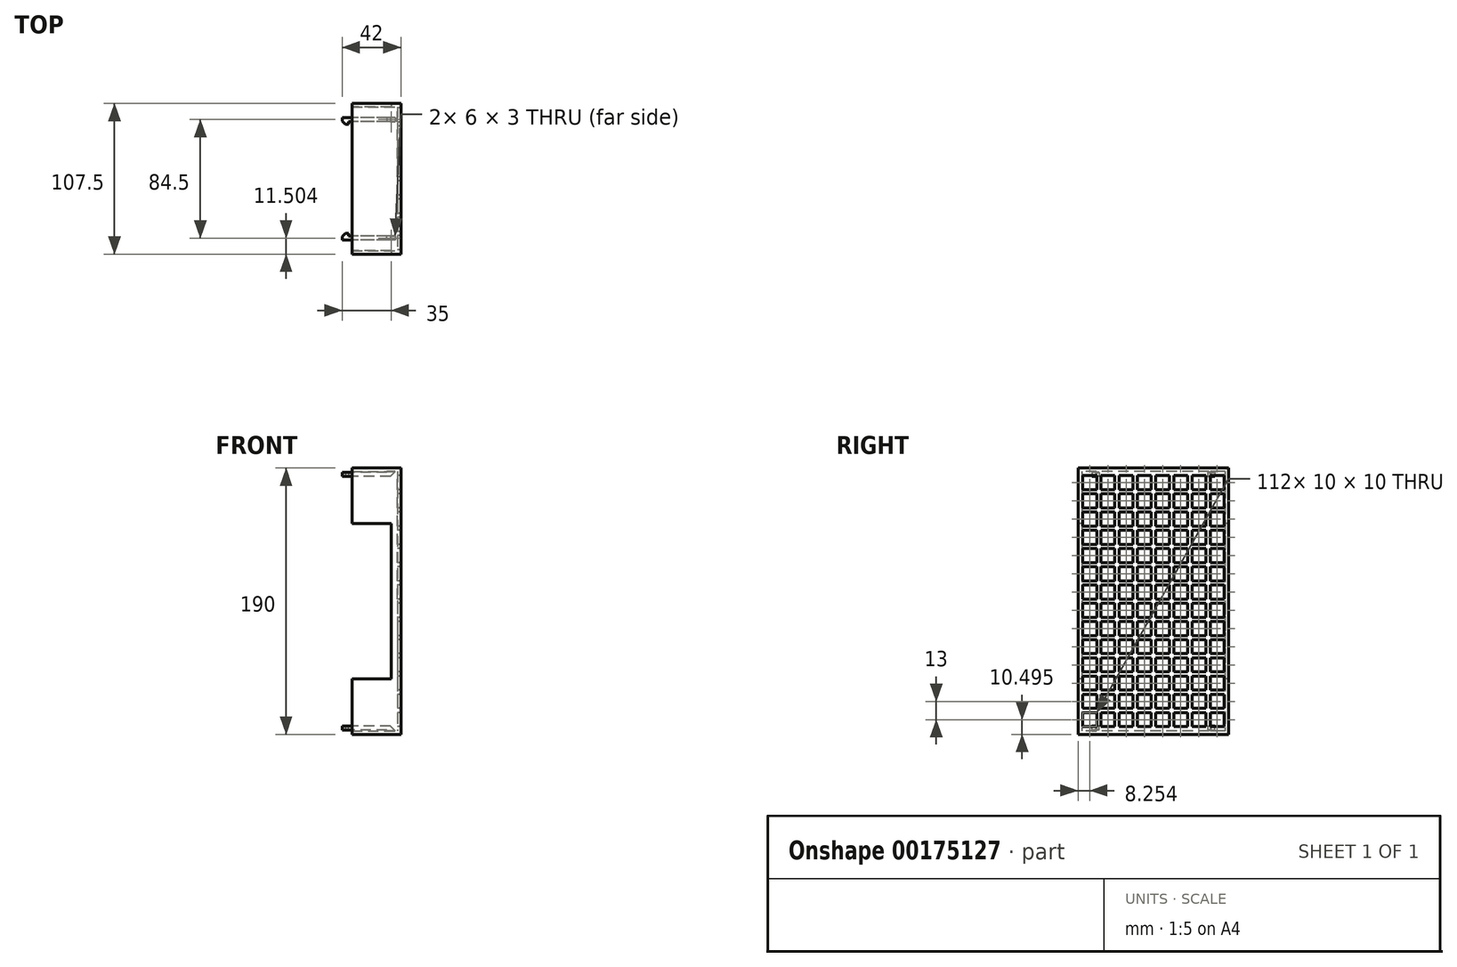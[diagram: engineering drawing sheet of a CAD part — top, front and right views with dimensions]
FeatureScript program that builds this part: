
annotation { "Feature Type Name" : "Feature", "Feature Type Description" : "" }
export const myFeature = defineFeature(function(context is Context, id is Id, definition is map)
    precondition{}
    {
        {
            var Q0;
            Q0=qCreatedBy(makeId("Right.planeOp"),FACE);
            var sketch = newSketch(context, id + "F0", { "sketchPlane" : qUnion([Q0])});
            skLineSegment(sketch, "E0.bottom", {"start": v(-54.49, 123.63) * mm, "end": v(53.01, 123.63) * mm});
            skLineSegment(sketch, "E0.top", {"start": v(-54.49, -66.37) * mm, "end": v(53.01, -66.37) * mm});
            skLineSegment(sketch, "E0.left", {"start": v(-54.49, 123.63) * mm, "end": v(-54.49, -66.37) * mm});
            skLineSegment(sketch, "E0.right", {"start": v(53.01, 123.63) * mm, "end": v(53.01, -66.37) * mm});
            skLineSegment(sketch, "E1.bottom", {"start": v(-2.24, 30.13) * mm, "end": v(-12.24, 30.13) * mm});
            skLineSegment(sketch, "E1.top", {"start": v(-2.24, 40.13) * mm, "end": v(-12.24, 40.13) * mm});
            skLineSegment(sketch, "E1.left", {"start": v(-2.24, 30.13) * mm, "end": v(-2.24, 40.13) * mm});
            skLineSegment(sketch, "E1.right", {"start": v(-12.24, 30.13) * mm, "end": v(-12.24, 40.13) * mm});
            skLineSegment(sketch, "E2.0.1.0", {"start": v(-2.24, 43.13) * mm, "end": v(-2.24, 53.13) * mm});
            skLineSegment(sketch, "E2.0.1.1", {"start": v(-12.24, 43.13) * mm, "end": v(-12.24, 53.13) * mm});
            skLineSegment(sketch, "E2.0.1.2", {"start": v(-2.24, 43.13) * mm, "end": v(-12.24, 43.13) * mm});
            skLineSegment(sketch, "E2.0.1.3", {"start": v(-2.24, 53.13) * mm, "end": v(-12.24, 53.13) * mm});
            skLineSegment(sketch, "E2.0.2.0", {"start": v(-2.24, 56.13) * mm, "end": v(-2.24, 66.13) * mm});
            skLineSegment(sketch, "E2.0.2.1", {"start": v(-12.24, 56.13) * mm, "end": v(-12.24, 66.13) * mm});
            skLineSegment(sketch, "E2.0.2.2", {"start": v(-2.24, 56.13) * mm, "end": v(-12.24, 56.13) * mm});
            skLineSegment(sketch, "E2.0.2.3", {"start": v(-2.24, 66.13) * mm, "end": v(-12.24, 66.13) * mm});
            skLineSegment(sketch, "E2.0.3.0", {"start": v(-2.24, 69.13) * mm, "end": v(-2.24, 79.13) * mm});
            skLineSegment(sketch, "E2.0.3.1", {"start": v(-12.24, 69.13) * mm, "end": v(-12.24, 79.13) * mm});
            skLineSegment(sketch, "E2.0.3.2", {"start": v(-2.24, 69.13) * mm, "end": v(-12.24, 69.13) * mm});
            skLineSegment(sketch, "E2.0.3.3", {"start": v(-2.24, 79.13) * mm, "end": v(-12.24, 79.13) * mm});
            skLineSegment(sketch, "E2.0.4.0", {"start": v(-2.24, 82.13) * mm, "end": v(-2.24, 92.13) * mm});
            skLineSegment(sketch, "E2.0.4.1", {"start": v(-12.24, 82.13) * mm, "end": v(-12.24, 92.13) * mm});
            skLineSegment(sketch, "E2.0.4.2", {"start": v(-2.24, 82.13) * mm, "end": v(-12.24, 82.13) * mm});
            skLineSegment(sketch, "E2.0.4.3", {"start": v(-2.24, 92.13) * mm, "end": v(-12.24, 92.13) * mm});
            skLineSegment(sketch, "E2.0.5.0", {"start": v(-2.24, 95.13) * mm, "end": v(-2.24, 105.13) * mm});
            skLineSegment(sketch, "E2.0.5.1", {"start": v(-12.24, 95.13) * mm, "end": v(-12.24, 105.13) * mm});
            skLineSegment(sketch, "E2.0.5.2", {"start": v(-2.24, 95.13) * mm, "end": v(-12.24, 95.13) * mm});
            skLineSegment(sketch, "E2.0.5.3", {"start": v(-2.24, 105.13) * mm, "end": v(-12.24, 105.13) * mm});
            skLineSegment(sketch, "E2.0.6.0", {"start": v(-2.24, 108.13) * mm, "end": v(-2.24, 118.13) * mm});
            skLineSegment(sketch, "E2.0.6.1", {"start": v(-12.24, 108.13) * mm, "end": v(-12.24, 118.13) * mm});
            skLineSegment(sketch, "E2.0.6.2", {"start": v(-2.24, 108.13) * mm, "end": v(-12.24, 108.13) * mm});
            skLineSegment(sketch, "E2.0.6.3", {"start": v(-2.24, 118.13) * mm, "end": v(-12.24, 118.13) * mm});
            skLineSegment(sketch, "E2.1.0.0", {"start": v(-15.24, 30.13) * mm, "end": v(-15.24, 40.13) * mm});
            skLineSegment(sketch, "E2.1.0.1", {"start": v(-25.24, 30.13) * mm, "end": v(-25.24, 40.13) * mm});
            skLineSegment(sketch, "E2.1.0.2", {"start": v(-15.24, 30.13) * mm, "end": v(-25.24, 30.13) * mm});
            skLineSegment(sketch, "E2.1.0.3", {"start": v(-15.24, 40.13) * mm, "end": v(-25.24, 40.13) * mm});
            skLineSegment(sketch, "E2.1.1.0", {"start": v(-15.24, 43.13) * mm, "end": v(-15.24, 53.13) * mm});
            skLineSegment(sketch, "E2.1.1.1", {"start": v(-25.24, 43.13) * mm, "end": v(-25.24, 53.13) * mm});
            skLineSegment(sketch, "E2.1.1.2", {"start": v(-15.24, 43.13) * mm, "end": v(-25.24, 43.13) * mm});
            skLineSegment(sketch, "E2.1.1.3", {"start": v(-15.24, 53.13) * mm, "end": v(-25.24, 53.13) * mm});
            skLineSegment(sketch, "E2.1.2.0", {"start": v(-15.24, 56.13) * mm, "end": v(-15.24, 66.13) * mm});
            skLineSegment(sketch, "E2.1.2.1", {"start": v(-25.24, 56.13) * mm, "end": v(-25.24, 66.13) * mm});
            skLineSegment(sketch, "E2.1.2.2", {"start": v(-15.24, 56.13) * mm, "end": v(-25.24, 56.13) * mm});
            skLineSegment(sketch, "E2.1.2.3", {"start": v(-15.24, 66.13) * mm, "end": v(-25.24, 66.13) * mm});
            skLineSegment(sketch, "E2.1.3.0", {"start": v(-15.24, 69.13) * mm, "end": v(-15.24, 79.13) * mm});
            skLineSegment(sketch, "E2.1.3.1", {"start": v(-25.24, 69.13) * mm, "end": v(-25.24, 79.13) * mm});
            skLineSegment(sketch, "E2.1.3.2", {"start": v(-15.24, 69.13) * mm, "end": v(-25.24, 69.13) * mm});
            skLineSegment(sketch, "E2.1.3.3", {"start": v(-15.24, 79.13) * mm, "end": v(-25.24, 79.13) * mm});
            skLineSegment(sketch, "E2.1.4.0", {"start": v(-15.24, 82.13) * mm, "end": v(-15.24, 92.13) * mm});
            skLineSegment(sketch, "E2.1.4.1", {"start": v(-25.24, 82.13) * mm, "end": v(-25.24, 92.13) * mm});
            skLineSegment(sketch, "E2.1.4.2", {"start": v(-15.24, 82.13) * mm, "end": v(-25.24, 82.13) * mm});
            skLineSegment(sketch, "E2.1.4.3", {"start": v(-15.24, 92.13) * mm, "end": v(-25.24, 92.13) * mm});
            skLineSegment(sketch, "E2.1.5.0", {"start": v(-15.24, 95.13) * mm, "end": v(-15.24, 105.13) * mm});
            skLineSegment(sketch, "E2.1.5.1", {"start": v(-25.24, 95.13) * mm, "end": v(-25.24, 105.13) * mm});
            skLineSegment(sketch, "E2.1.5.2", {"start": v(-15.24, 95.13) * mm, "end": v(-25.24, 95.13) * mm});
            skLineSegment(sketch, "E2.1.5.3", {"start": v(-15.24, 105.13) * mm, "end": v(-25.24, 105.13) * mm});
            skLineSegment(sketch, "E2.1.6.0", {"start": v(-15.24, 108.13) * mm, "end": v(-15.24, 118.13) * mm});
            skLineSegment(sketch, "E2.1.6.1", {"start": v(-25.24, 108.13) * mm, "end": v(-25.24, 118.13) * mm});
            skLineSegment(sketch, "E2.1.6.2", {"start": v(-15.24, 108.13) * mm, "end": v(-25.24, 108.13) * mm});
            skLineSegment(sketch, "E2.1.6.3", {"start": v(-15.24, 118.13) * mm, "end": v(-25.24, 118.13) * mm});
            skLineSegment(sketch, "E2.2.0.0", {"start": v(-28.24, 30.13) * mm, "end": v(-28.24, 40.13) * mm});
            skLineSegment(sketch, "E2.2.0.1", {"start": v(-38.24, 30.13) * mm, "end": v(-38.24, 40.13) * mm});
            skLineSegment(sketch, "E2.2.0.2", {"start": v(-28.24, 30.13) * mm, "end": v(-38.24, 30.13) * mm});
            skLineSegment(sketch, "E2.2.0.3", {"start": v(-28.24, 40.13) * mm, "end": v(-38.24, 40.13) * mm});
            skLineSegment(sketch, "E2.2.1.0", {"start": v(-28.24, 43.13) * mm, "end": v(-28.24, 53.13) * mm});
            skLineSegment(sketch, "E2.2.1.1", {"start": v(-38.24, 43.13) * mm, "end": v(-38.24, 53.13) * mm});
            skLineSegment(sketch, "E2.2.1.2", {"start": v(-28.24, 43.13) * mm, "end": v(-38.24, 43.13) * mm});
            skLineSegment(sketch, "E2.2.1.3", {"start": v(-28.24, 53.13) * mm, "end": v(-38.24, 53.13) * mm});
            skLineSegment(sketch, "E2.2.2.0", {"start": v(-28.24, 56.13) * mm, "end": v(-28.24, 66.13) * mm});
            skLineSegment(sketch, "E2.2.2.1", {"start": v(-38.24, 56.13) * mm, "end": v(-38.24, 66.13) * mm});
            skLineSegment(sketch, "E2.2.2.2", {"start": v(-28.24, 56.13) * mm, "end": v(-38.24, 56.13) * mm});
            skLineSegment(sketch, "E2.2.2.3", {"start": v(-28.24, 66.13) * mm, "end": v(-38.24, 66.13) * mm});
            skLineSegment(sketch, "E2.2.3.0", {"start": v(-28.24, 69.13) * mm, "end": v(-28.24, 79.13) * mm});
            skLineSegment(sketch, "E2.2.3.1", {"start": v(-38.24, 69.13) * mm, "end": v(-38.24, 79.13) * mm});
            skLineSegment(sketch, "E2.2.3.2", {"start": v(-28.24, 69.13) * mm, "end": v(-38.24, 69.13) * mm});
            skLineSegment(sketch, "E2.2.3.3", {"start": v(-28.24, 79.13) * mm, "end": v(-38.24, 79.13) * mm});
            skLineSegment(sketch, "E2.2.4.0", {"start": v(-28.24, 82.13) * mm, "end": v(-28.24, 92.13) * mm});
            skLineSegment(sketch, "E2.2.4.1", {"start": v(-38.24, 82.13) * mm, "end": v(-38.24, 92.13) * mm});
            skLineSegment(sketch, "E2.2.4.2", {"start": v(-28.24, 82.13) * mm, "end": v(-38.24, 82.13) * mm});
            skLineSegment(sketch, "E2.2.4.3", {"start": v(-28.24, 92.13) * mm, "end": v(-38.24, 92.13) * mm});
            skLineSegment(sketch, "E2.2.5.0", {"start": v(-28.24, 95.13) * mm, "end": v(-28.24, 105.13) * mm});
            skLineSegment(sketch, "E2.2.5.1", {"start": v(-38.24, 95.13) * mm, "end": v(-38.24, 105.13) * mm});
            skLineSegment(sketch, "E2.2.5.2", {"start": v(-28.24, 95.13) * mm, "end": v(-38.24, 95.13) * mm});
            skLineSegment(sketch, "E2.2.5.3", {"start": v(-28.24, 105.13) * mm, "end": v(-38.24, 105.13) * mm});
            skLineSegment(sketch, "E2.2.6.0", {"start": v(-28.24, 108.13) * mm, "end": v(-28.24, 118.13) * mm});
            skLineSegment(sketch, "E2.2.6.1", {"start": v(-38.24, 108.13) * mm, "end": v(-38.24, 118.13) * mm});
            skLineSegment(sketch, "E2.2.6.2", {"start": v(-28.24, 108.13) * mm, "end": v(-38.24, 108.13) * mm});
            skLineSegment(sketch, "E2.2.6.3", {"start": v(-28.24, 118.13) * mm, "end": v(-38.24, 118.13) * mm});
            skLineSegment(sketch, "E2.3.0.0", {"start": v(-41.24, 30.13) * mm, "end": v(-41.24, 40.13) * mm});
            skLineSegment(sketch, "E2.3.0.1", {"start": v(-51.24, 30.13) * mm, "end": v(-51.24, 40.13) * mm});
            skLineSegment(sketch, "E2.3.0.2", {"start": v(-41.24, 30.13) * mm, "end": v(-51.24, 30.13) * mm});
            skLineSegment(sketch, "E2.3.0.3", {"start": v(-41.24, 40.13) * mm, "end": v(-51.24, 40.13) * mm});
            skLineSegment(sketch, "E2.3.1.0", {"start": v(-41.24, 43.13) * mm, "end": v(-41.24, 53.13) * mm});
            skLineSegment(sketch, "E2.3.1.1", {"start": v(-51.24, 43.13) * mm, "end": v(-51.24, 53.13) * mm});
            skLineSegment(sketch, "E2.3.1.2", {"start": v(-41.24, 43.13) * mm, "end": v(-51.24, 43.13) * mm});
            skLineSegment(sketch, "E2.3.1.3", {"start": v(-41.24, 53.13) * mm, "end": v(-51.24, 53.13) * mm});
            skLineSegment(sketch, "E2.3.2.0", {"start": v(-41.24, 56.13) * mm, "end": v(-41.24, 66.13) * mm});
            skLineSegment(sketch, "E2.3.2.1", {"start": v(-51.24, 56.13) * mm, "end": v(-51.24, 66.13) * mm});
            skLineSegment(sketch, "E2.3.2.2", {"start": v(-41.24, 56.13) * mm, "end": v(-51.24, 56.13) * mm});
            skLineSegment(sketch, "E2.3.2.3", {"start": v(-41.24, 66.13) * mm, "end": v(-51.24, 66.13) * mm});
            skLineSegment(sketch, "E2.3.3.0", {"start": v(-41.24, 69.13) * mm, "end": v(-41.24, 79.13) * mm});
            skLineSegment(sketch, "E2.3.3.1", {"start": v(-51.24, 69.13) * mm, "end": v(-51.24, 79.13) * mm});
            skLineSegment(sketch, "E2.3.3.2", {"start": v(-41.24, 69.13) * mm, "end": v(-51.24, 69.13) * mm});
            skLineSegment(sketch, "E2.3.3.3", {"start": v(-41.24, 79.13) * mm, "end": v(-51.24, 79.13) * mm});
            skLineSegment(sketch, "E2.3.4.0", {"start": v(-41.24, 82.13) * mm, "end": v(-41.24, 92.13) * mm});
            skLineSegment(sketch, "E2.3.4.1", {"start": v(-51.24, 82.13) * mm, "end": v(-51.24, 92.13) * mm});
            skLineSegment(sketch, "E2.3.4.2", {"start": v(-41.24, 82.13) * mm, "end": v(-51.24, 82.13) * mm});
            skLineSegment(sketch, "E2.3.4.3", {"start": v(-41.24, 92.13) * mm, "end": v(-51.24, 92.13) * mm});
            skLineSegment(sketch, "E2.3.5.0", {"start": v(-41.24, 95.13) * mm, "end": v(-41.24, 105.13) * mm});
            skLineSegment(sketch, "E2.3.5.1", {"start": v(-51.24, 95.13) * mm, "end": v(-51.24, 105.13) * mm});
            skLineSegment(sketch, "E2.3.5.2", {"start": v(-41.24, 95.13) * mm, "end": v(-51.24, 95.13) * mm});
            skLineSegment(sketch, "E2.3.5.3", {"start": v(-41.24, 105.13) * mm, "end": v(-51.24, 105.13) * mm});
            skLineSegment(sketch, "E2.3.6.0", {"start": v(-41.24, 108.13) * mm, "end": v(-41.24, 118.13) * mm});
            skLineSegment(sketch, "E2.3.6.1", {"start": v(-51.24, 108.13) * mm, "end": v(-51.24, 118.13) * mm});
            skLineSegment(sketch, "E2.3.6.2", {"start": v(-41.24, 108.13) * mm, "end": v(-51.24, 108.13) * mm});
            skLineSegment(sketch, "E2.3.6.3", {"start": v(-41.24, 118.13) * mm, "end": v(-51.24, 118.13) * mm});
            skLineSegment(sketch, "E2.direction1", {"start": v(-12.24, 30.13) * mm, "end": v(-25.24, 30.13) * mm, "construction": true});
            skLineSegment(sketch, "E2.direction2", {"start": v(-12.24, 30.13) * mm, "end": v(-12.24, 43.13) * mm, "construction": true});
            skLineSegment(sketch, "E3.MirrorCS", {"start": v(10.76, 30.13) * mm, "end": v(10.76, 40.13) * mm});
            skLineSegment(sketch, "E4.MirrorCS", {"start": v(26.76, 30.13) * mm, "end": v(26.76, 40.13) * mm});
            skLineSegment(sketch, "E5.MirrorCS", {"start": v(13.76, 43.13) * mm, "end": v(23.76, 43.13) * mm});
            skLineSegment(sketch, "E6.MirrorCS", {"start": v(13.76, 40.13) * mm, "end": v(23.76, 40.13) * mm});
            skLineSegment(sketch, "E7.MirrorCS", {"start": v(13.76, 30.13) * mm, "end": v(23.76, 30.13) * mm});
            skLineSegment(sketch, "E8.MirrorCS", {"start": v(23.76, 30.13) * mm, "end": v(23.76, 40.13) * mm});
            skLineSegment(sketch, "E9.MirrorCS", {"start": v(26.76, 79.13) * mm, "end": v(36.76, 79.13) * mm});
            skLineSegment(sketch, "E10.MirrorCS", {"start": v(13.76, 118.13) * mm, "end": v(23.76, 118.13) * mm});
            skLineSegment(sketch, "E11.MirrorCS", {"start": v(13.76, 66.13) * mm, "end": v(23.76, 66.13) * mm});
            skLineSegment(sketch, "E12.MirrorCS", {"start": v(0.76, 105.13) * mm, "end": v(10.76, 105.13) * mm});
            skLineSegment(sketch, "E13.MirrorCS", {"start": v(39.76, 92.13) * mm, "end": v(49.76, 92.13) * mm});
            skLineSegment(sketch, "E14.MirrorCS", {"start": v(39.76, 40.13) * mm, "end": v(49.76, 40.13) * mm});
            skLineSegment(sketch, "E15.MirrorCS", {"start": v(10.76, 43.13) * mm, "end": v(10.76, 53.13) * mm});
            skLineSegment(sketch, "E16.MirrorCS", {"start": v(0.76, 43.13) * mm, "end": v(10.76, 43.13) * mm});
            skLineSegment(sketch, "E17.MirrorCS", {"start": v(0.76, 53.13) * mm, "end": v(10.76, 53.13) * mm});
            skLineSegment(sketch, "E18.MirrorCS", {"start": v(0.76, 95.13) * mm, "end": v(10.76, 95.13) * mm});
            skLineSegment(sketch, "E19.MirrorCS", {"start": v(39.76, 82.13) * mm, "end": v(49.76, 82.13) * mm});
            skLineSegment(sketch, "E20.MirrorCS", {"start": v(39.76, 30.13) * mm, "end": v(49.76, 30.13) * mm});
            skLineSegment(sketch, "E21.MirrorCS", {"start": v(0.76, 30.13) * mm, "end": v(10.76, 30.13) * mm});
            skLineSegment(sketch, "E22.MirrorCS", {"start": v(0.76, 40.13) * mm, "end": v(10.76, 40.13) * mm});
            skLineSegment(sketch, "E23.MirrorCS", {"start": v(0.76, 30.13) * mm, "end": v(0.76, 40.13) * mm});
            skLineSegment(sketch, "E24.MirrorCS", {"start": v(0.76, 43.13) * mm, "end": v(0.76, 53.13) * mm});
            skLineSegment(sketch, "E25.MirrorCS", {"start": v(39.76, 95.13) * mm, "end": v(39.76, 105.13) * mm});
            skLineSegment(sketch, "E26.MirrorCS", {"start": v(39.76, 43.13) * mm, "end": v(39.76, 53.13) * mm});
            skLineSegment(sketch, "E27.MirrorCS", {"start": v(0.76, 56.13) * mm, "end": v(0.76, 66.13) * mm});
            skLineSegment(sketch, "E28.MirrorCS", {"start": v(26.76, 82.13) * mm, "end": v(26.76, 92.13) * mm});
            skLineSegment(sketch, "E29.MirrorCS", {"start": v(49.76, 95.13) * mm, "end": v(49.76, 105.13) * mm});
            skLineSegment(sketch, "E30.MirrorCS", {"start": v(39.76, 95.13) * mm, "end": v(49.76, 95.13) * mm});
            skLineSegment(sketch, "E31.MirrorCS", {"start": v(26.76, 82.13) * mm, "end": v(36.76, 82.13) * mm});
            skLineSegment(sketch, "E32.MirrorCS", {"start": v(0.76, 56.13) * mm, "end": v(10.76, 56.13) * mm});
            skLineSegment(sketch, "E33.MirrorCS", {"start": v(23.76, 69.13) * mm, "end": v(23.76, 79.13) * mm});
            skLineSegment(sketch, "E34.MirrorCS", {"start": v(49.76, 43.13) * mm, "end": v(49.76, 53.13) * mm});
            skLineSegment(sketch, "E35.MirrorCS", {"start": v(36.76, 82.13) * mm, "end": v(36.76, 92.13) * mm});
            skLineSegment(sketch, "E36.MirrorCS", {"start": v(13.76, 69.13) * mm, "end": v(23.76, 69.13) * mm});
            skLineSegment(sketch, "E37.MirrorCS", {"start": v(10.76, 56.13) * mm, "end": v(10.76, 66.13) * mm});
            skLineSegment(sketch, "E38.MirrorCS", {"start": v(0.76, 108.13) * mm, "end": v(10.76, 108.13) * mm});
            skLineSegment(sketch, "E39.MirrorCS", {"start": v(39.76, 43.13) * mm, "end": v(49.76, 43.13) * mm});
            skLineSegment(sketch, "E40.MirrorCS", {"start": v(36.76, 30.13) * mm, "end": v(36.76, 40.13) * mm});
            skLineSegment(sketch, "E41.MirrorCS", {"start": v(0.76, 108.13) * mm, "end": v(0.76, 118.13) * mm});
            skLineSegment(sketch, "E42.MirrorCS", {"start": v(13.76, 56.13) * mm, "end": v(23.76, 56.13) * mm});
            skLineSegment(sketch, "E43.MirrorCS", {"start": v(13.76, 69.13) * mm, "end": v(13.76, 79.13) * mm});
            skLineSegment(sketch, "E44.MirrorCS", {"start": v(26.76, 30.13) * mm, "end": v(36.76, 30.13) * mm});
            skLineSegment(sketch, "E45.MirrorCS", {"start": v(10.76, 108.13) * mm, "end": v(10.76, 118.13) * mm});
            skLineSegment(sketch, "E46.MirrorCS", {"start": v(49.76, 82.13) * mm, "end": v(49.76, 92.13) * mm});
            skLineSegment(sketch, "E47.MirrorCS", {"start": v(49.76, 30.13) * mm, "end": v(49.76, 40.13) * mm});
            skLineSegment(sketch, "E48.MirrorCS", {"start": v(13.76, 108.13) * mm, "end": v(13.76, 118.13) * mm});
            skLineSegment(sketch, "E49.MirrorCS", {"start": v(13.76, 56.13) * mm, "end": v(13.76, 66.13) * mm});
            skLineSegment(sketch, "E50.MirrorCS", {"start": v(0.76, 95.13) * mm, "end": v(0.76, 105.13) * mm});
            skLineSegment(sketch, "E51.MirrorCS", {"start": v(39.76, 82.13) * mm, "end": v(39.76, 92.13) * mm});
            skLineSegment(sketch, "E52.MirrorCS", {"start": v(39.76, 30.13) * mm, "end": v(39.76, 40.13) * mm});
            skLineSegment(sketch, "E53.MirrorCS", {"start": v(26.76, 69.13) * mm, "end": v(26.76, 79.13) * mm});
            skLineSegment(sketch, "E54.MirrorCS", {"start": v(26.76, 69.13) * mm, "end": v(36.76, 69.13) * mm});
            skLineSegment(sketch, "E55.MirrorCS", {"start": v(13.76, 108.13) * mm, "end": v(23.76, 108.13) * mm});
            skLineSegment(sketch, "E56.MirrorCS", {"start": v(10.76, 95.13) * mm, "end": v(10.76, 105.13) * mm});
            skLineSegment(sketch, "E57.MirrorCS", {"start": v(23.76, 56.13) * mm, "end": v(23.76, 66.13) * mm});
            skLineSegment(sketch, "E58.MirrorCS", {"start": v(23.76, 108.13) * mm, "end": v(23.76, 118.13) * mm});
            skLineSegment(sketch, "E59.MirrorCS", {"start": v(36.76, 69.13) * mm, "end": v(36.76, 79.13) * mm});
            skLineSegment(sketch, "E60.MirrorCS", {"start": v(26.76, 66.13) * mm, "end": v(36.76, 66.13) * mm});
            skLineSegment(sketch, "E61.MirrorCS", {"start": v(26.76, 118.13) * mm, "end": v(36.76, 118.13) * mm});
            skLineSegment(sketch, "E62.MirrorCS", {"start": v(39.76, 79.13) * mm, "end": v(49.76, 79.13) * mm});
            skLineSegment(sketch, "E63.MirrorCS", {"start": v(0.76, 92.13) * mm, "end": v(10.76, 92.13) * mm});
            skLineSegment(sketch, "E64.MirrorCS", {"start": v(13.76, 53.13) * mm, "end": v(23.76, 53.13) * mm});
            skLineSegment(sketch, "E65.MirrorCS", {"start": v(13.76, 105.13) * mm, "end": v(23.76, 105.13) * mm});
            skLineSegment(sketch, "E66.MirrorCS", {"start": v(26.76, 56.13) * mm, "end": v(36.76, 56.13) * mm});
            skLineSegment(sketch, "E67.MirrorCS", {"start": v(26.76, 108.13) * mm, "end": v(36.76, 108.13) * mm});
            skLineSegment(sketch, "E68.MirrorCS", {"start": v(39.76, 69.13) * mm, "end": v(49.76, 69.13) * mm});
            skLineSegment(sketch, "E69.MirrorCS", {"start": v(0.76, 82.13) * mm, "end": v(10.76, 82.13) * mm});
            skLineSegment(sketch, "E70.MirrorCS", {"start": v(13.76, 95.13) * mm, "end": v(23.76, 95.13) * mm});
            skLineSegment(sketch, "E71.MirrorCS", {"start": v(36.76, 56.13) * mm, "end": v(36.76, 66.13) * mm});
            skLineSegment(sketch, "E72.MirrorCS", {"start": v(36.76, 108.13) * mm, "end": v(36.76, 118.13) * mm});
            skLineSegment(sketch, "E73.MirrorCS", {"start": v(49.76, 69.13) * mm, "end": v(49.76, 79.13) * mm});
            skLineSegment(sketch, "E74.MirrorCS", {"start": v(10.76, 30.13) * mm, "end": v(10.76, 43.13) * mm, "construction": true});
            skLineSegment(sketch, "E75.MirrorCS", {"start": v(10.76, 82.13) * mm, "end": v(10.76, 92.13) * mm});
            skLineSegment(sketch, "E76.MirrorCS", {"start": v(23.76, 43.13) * mm, "end": v(23.76, 53.13) * mm});
            skLineSegment(sketch, "E77.MirrorCS", {"start": v(23.76, 95.13) * mm, "end": v(23.76, 105.13) * mm});
            skLineSegment(sketch, "E78.MirrorCS", {"start": v(26.76, 56.13) * mm, "end": v(26.76, 66.13) * mm});
            skLineSegment(sketch, "E79.MirrorCS", {"start": v(26.76, 108.13) * mm, "end": v(26.76, 118.13) * mm});
            skLineSegment(sketch, "E80.MirrorCS", {"start": v(39.76, 69.13) * mm, "end": v(39.76, 79.13) * mm});
            skLineSegment(sketch, "E81.MirrorCS", {"start": v(10.76, 30.13) * mm, "end": v(23.76, 30.13) * mm, "construction": true});
            skLineSegment(sketch, "E82.MirrorCS", {"start": v(0.76, 82.13) * mm, "end": v(0.76, 92.13) * mm});
            skLineSegment(sketch, "E83.MirrorCS", {"start": v(13.76, 43.13) * mm, "end": v(13.76, 53.13) * mm});
            skLineSegment(sketch, "E84.MirrorCS", {"start": v(13.76, 95.13) * mm, "end": v(13.76, 105.13) * mm});
            skLineSegment(sketch, "E85.MirrorCS", {"start": v(26.76, 105.13) * mm, "end": v(36.76, 105.13) * mm});
            skLineSegment(sketch, "E86.MirrorCS", {"start": v(26.76, 53.13) * mm, "end": v(36.76, 53.13) * mm});
            skLineSegment(sketch, "E87.MirrorCS", {"start": v(39.76, 66.13) * mm, "end": v(49.76, 66.13) * mm});
            skLineSegment(sketch, "E88.MirrorCS", {"start": v(39.76, 118.13) * mm, "end": v(49.76, 118.13) * mm});
            skLineSegment(sketch, "E89.MirrorCS", {"start": v(0.76, 79.13) * mm, "end": v(10.76, 79.13) * mm});
            skLineSegment(sketch, "E90.MirrorCS", {"start": v(13.76, 92.13) * mm, "end": v(23.76, 92.13) * mm});
            skLineSegment(sketch, "E91.MirrorCS", {"start": v(39.76, 56.13) * mm, "end": v(49.76, 56.13) * mm});
            skLineSegment(sketch, "E92.MirrorCS", {"start": v(39.76, 108.13) * mm, "end": v(49.76, 108.13) * mm});
            skLineSegment(sketch, "E93.MirrorCS", {"start": v(13.76, 82.13) * mm, "end": v(23.76, 82.13) * mm});
            skLineSegment(sketch, "E94.MirrorCS", {"start": v(26.76, 43.13) * mm, "end": v(36.76, 43.13) * mm});
            skLineSegment(sketch, "E95.MirrorCS", {"start": v(26.76, 95.13) * mm, "end": v(36.76, 95.13) * mm});
            skLineSegment(sketch, "E96.MirrorCS", {"start": v(0.76, 69.13) * mm, "end": v(10.76, 69.13) * mm});
            skLineSegment(sketch, "E97.MirrorCS", {"start": v(49.76, 56.13) * mm, "end": v(49.76, 66.13) * mm});
            skLineSegment(sketch, "E98.MirrorCS", {"start": v(49.76, 108.13) * mm, "end": v(49.76, 118.13) * mm});
            skLineSegment(sketch, "E99.MirrorCS", {"start": v(23.76, 82.13) * mm, "end": v(23.76, 92.13) * mm});
            skLineSegment(sketch, "E100.MirrorCS", {"start": v(36.76, 43.13) * mm, "end": v(36.76, 53.13) * mm});
            skLineSegment(sketch, "E101.MirrorCS", {"start": v(36.76, 95.13) * mm, "end": v(36.76, 105.13) * mm});
            skLineSegment(sketch, "E102.MirrorCS", {"start": v(10.76, 69.13) * mm, "end": v(10.76, 79.13) * mm});
            skLineSegment(sketch, "E103.MirrorCS", {"start": v(39.76, 56.13) * mm, "end": v(39.76, 66.13) * mm});
            skLineSegment(sketch, "E104.MirrorCS", {"start": v(39.76, 108.13) * mm, "end": v(39.76, 118.13) * mm});
            skLineSegment(sketch, "E105.MirrorCS", {"start": v(13.76, 30.13) * mm, "end": v(13.76, 40.13) * mm});
            skLineSegment(sketch, "E106.MirrorCS", {"start": v(13.76, 82.13) * mm, "end": v(13.76, 92.13) * mm});
            skLineSegment(sketch, "E107.MirrorCS", {"start": v(26.76, 43.13) * mm, "end": v(26.76, 53.13) * mm});
            skLineSegment(sketch, "E108.MirrorCS", {"start": v(26.76, 95.13) * mm, "end": v(26.76, 105.13) * mm});
            skLineSegment(sketch, "E109.MirrorCS", {"start": v(0.76, 69.13) * mm, "end": v(0.76, 79.13) * mm});
            skLineSegment(sketch, "E110.MirrorCS", {"start": v(39.76, 53.13) * mm, "end": v(49.76, 53.13) * mm});
            skLineSegment(sketch, "E111.MirrorCS", {"start": v(39.76, 105.13) * mm, "end": v(49.76, 105.13) * mm});
            skLineSegment(sketch, "E112.MirrorCS", {"start": v(0.76, 118.13) * mm, "end": v(10.76, 118.13) * mm});
            skLineSegment(sketch, "E113.MirrorCS", {"start": v(13.76, 79.13) * mm, "end": v(23.76, 79.13) * mm});
            skLineSegment(sketch, "E114.MirrorCS", {"start": v(26.76, 40.13) * mm, "end": v(36.76, 40.13) * mm});
            skLineSegment(sketch, "E115.MirrorCS", {"start": v(26.76, 92.13) * mm, "end": v(36.76, 92.13) * mm});
            skLineSegment(sketch, "E116.MirrorCS", {"start": v(0.76, 66.13) * mm, "end": v(10.76, 66.13) * mm});
            skLineSegment(sketch, "E117.MirrorCS", {"start": v(-15.24, 17.13) * mm, "end": v(-25.24, 17.13) * mm});
            skLineSegment(sketch, "E118.MirrorCS", {"start": v(-15.24, 27.13) * mm, "end": v(-25.24, 27.13) * mm});
            skLineSegment(sketch, "E119.MirrorCS", {"start": v(13.76, 27.13) * mm, "end": v(23.76, 27.13) * mm});
            skLineSegment(sketch, "E120.MirrorCS", {"start": v(-15.24, 1.13) * mm, "end": v(-25.24, 1.13) * mm});
            skLineSegment(sketch, "E121.MirrorCS", {"start": v(-15.24, 14.13) * mm, "end": v(-25.24, 14.13) * mm});
            skLineSegment(sketch, "E122.MirrorCS", {"start": v(10.76, 27.13) * mm, "end": v(10.76, 17.13) * mm});
            skLineSegment(sketch, "E123.MirrorCS", {"start": v(-15.24, 4.13) * mm, "end": v(-25.24, 4.13) * mm});
            skLineSegment(sketch, "E124.MirrorCS", {"start": v(-28.24, 27.13) * mm, "end": v(-28.24, 17.13) * mm});
            skLineSegment(sketch, "E125.MirrorCS", {"start": v(-2.24, 17.13) * mm, "end": v(-12.24, 17.13) * mm});
            skLineSegment(sketch, "E126.MirrorCS", {"start": v(-2.24, 27.13) * mm, "end": v(-2.24, 17.13) * mm});
            skLineSegment(sketch, "E127.MirrorCS", {"start": v(-12.24, 27.13) * mm, "end": v(-12.24, 17.13) * mm});
            skLineSegment(sketch, "E128.MirrorCS", {"start": v(-2.24, 14.13) * mm, "end": v(-12.24, 14.13) * mm});
            skLineSegment(sketch, "E129.MirrorCS", {"start": v(-25.24, 27.13) * mm, "end": v(-25.24, 17.13) * mm});
            skLineSegment(sketch, "E130.MirrorCS", {"start": v(-15.24, 14.13) * mm, "end": v(-15.24, 4.13) * mm});
            skLineSegment(sketch, "E131.MirrorCS", {"start": v(-12.24, 27.13) * mm, "end": v(-12.24, 14.13) * mm, "construction": true});
            skLineSegment(sketch, "E132.MirrorCS", {"start": v(-15.24, -37.87) * mm, "end": v(-15.24, -47.87) * mm});
            skLineSegment(sketch, "E133.MirrorCS", {"start": v(-28.24, 1.13) * mm, "end": v(-28.24, -8.87) * mm});
            skLineSegment(sketch, "E134.MirrorCS", {"start": v(-28.24, -50.87) * mm, "end": v(-28.24, -60.87) * mm});
            skLineSegment(sketch, "E135.MirrorCS", {"start": v(-2.24, -24.87) * mm, "end": v(-2.24, -34.87) * mm});
            skLineSegment(sketch, "E136.MirrorCS", {"start": v(13.76, -47.87) * mm, "end": v(23.76, -47.87) * mm});
            skLineSegment(sketch, "E137.MirrorCS", {"start": v(-15.24, -50.87) * mm, "end": v(-25.24, -50.87) * mm});
            skLineSegment(sketch, "E138.MirrorCS", {"start": v(13.76, -50.87) * mm, "end": v(13.76, -60.87) * mm});
            skLineSegment(sketch, "E139.MirrorCS", {"start": v(13.76, -21.87) * mm, "end": v(23.76, -21.87) * mm});
            skLineSegment(sketch, "E140.MirrorCS", {"start": v(0.76, -60.87) * mm, "end": v(10.76, -60.87) * mm});
            skLineSegment(sketch, "E141.MirrorCS", {"start": v(13.76, 4.13) * mm, "end": v(23.76, 4.13) * mm});
            skLineSegment(sketch, "E142.MirrorCS", {"start": v(39.76, -11.87) * mm, "end": v(39.76, -21.87) * mm});
            skLineSegment(sketch, "E143.MirrorCS", {"start": v(0.76, -11.87) * mm, "end": v(10.76, -11.87) * mm});
            skLineSegment(sketch, "E144.MirrorCS", {"start": v(-41.24, -8.87) * mm, "end": v(-51.24, -8.87) * mm});
            skLineSegment(sketch, "E145.MirrorCS", {"start": v(-41.24, -11.87) * mm, "end": v(-41.24, -21.87) * mm});
            skLineSegment(sketch, "E146.MirrorCS", {"start": v(-12.24, 27.13) * mm, "end": v(-25.24, 27.13) * mm, "construction": true});
            skLineSegment(sketch, "E147.MirrorCS", {"start": v(-41.24, -60.87) * mm, "end": v(-51.24, -60.87) * mm});
            skLineSegment(sketch, "E148.MirrorCS", {"start": v(0.76, 14.13) * mm, "end": v(10.76, 14.13) * mm});
            skLineSegment(sketch, "E149.MirrorCS", {"start": v(0.76, 1.13) * mm, "end": v(10.76, 1.13) * mm});
            skLineSegment(sketch, "E150.MirrorCS", {"start": v(0.76, 4.13) * mm, "end": v(10.76, 4.13) * mm});
            skLineSegment(sketch, "E151.MirrorCS", {"start": v(-15.24, -34.87) * mm, "end": v(-25.24, -34.87) * mm});
            skLineSegment(sketch, "E152.MirrorCS", {"start": v(-28.24, 4.13) * mm, "end": v(-38.24, 4.13) * mm});
            skLineSegment(sketch, "E153.MirrorCS", {"start": v(-28.24, -47.87) * mm, "end": v(-38.24, -47.87) * mm});
            skLineSegment(sketch, "E154.MirrorCS", {"start": v(-2.24, -21.87) * mm, "end": v(-12.24, -21.87) * mm});
            skLineSegment(sketch, "E155.MirrorCS", {"start": v(0.76, -37.87) * mm, "end": v(10.76, -37.87) * mm});
            skLineSegment(sketch, "E156.MirrorCS", {"start": v(-25.24, 14.13) * mm, "end": v(-25.24, 4.13) * mm});
            skLineSegment(sketch, "E157.MirrorCS", {"start": v(10.76, 27.13) * mm, "end": v(23.76, 27.13) * mm, "construction": true});
            skLineSegment(sketch, "E158.MirrorCS", {"start": v(49.76, 1.13) * mm, "end": v(49.76, -8.87) * mm});
            skLineSegment(sketch, "E159.MirrorCS", {"start": v(26.76, -50.87) * mm, "end": v(26.76, -60.87) * mm});
            skLineSegment(sketch, "E160.MirrorCS", {"start": v(26.76, -37.87) * mm, "end": v(36.76, -37.87) * mm});
            skLineSegment(sketch, "E161.MirrorCS", {"start": v(-41.24, 1.13) * mm, "end": v(-51.24, 1.13) * mm});
            skLineSegment(sketch, "E162.MirrorCS", {"start": v(0.76, 27.13) * mm, "end": v(0.76, 17.13) * mm});
            skLineSegment(sketch, "E163.MirrorCS", {"start": v(13.76, 1.13) * mm, "end": v(13.76, -8.87) * mm});
            skLineSegment(sketch, "E164.MirrorCS", {"start": v(0.76, -34.87) * mm, "end": v(10.76, -34.87) * mm});
            skLineSegment(sketch, "E165.MirrorCS", {"start": v(-41.24, -50.87) * mm, "end": v(-51.24, -50.87) * mm});
            skLineSegment(sketch, "E166.MirrorCS", {"start": v(26.76, -24.87) * mm, "end": v(36.76, -24.87) * mm});
            skLineSegment(sketch, "E167.MirrorCS", {"start": v(-28.24, -11.87) * mm, "end": v(-38.24, -11.87) * mm});
            skLineSegment(sketch, "E168.MirrorCS", {"start": v(23.76, -11.87) * mm, "end": v(23.76, -21.87) * mm});
            skLineSegment(sketch, "E169.MirrorCS", {"start": v(36.76, 1.13) * mm, "end": v(36.76, -8.87) * mm});
            skLineSegment(sketch, "E170.MirrorCS", {"start": v(-28.24, -37.87) * mm, "end": v(-38.24, -37.87) * mm});
            skLineSegment(sketch, "E171.MirrorCS", {"start": v(10.76, 14.13) * mm, "end": v(10.76, 4.13) * mm});
            skLineSegment(sketch, "E172.MirrorCS", {"start": v(-41.24, -24.87) * mm, "end": v(-51.24, -24.87) * mm});
            skLineSegment(sketch, "E173.MirrorCS", {"start": v(49.76, 27.13) * mm, "end": v(49.76, 17.13) * mm});
            skLineSegment(sketch, "E174.MirrorCS", {"start": v(39.76, 1.13) * mm, "end": v(39.76, -8.87) * mm});
            skLineSegment(sketch, "E175.MirrorCS", {"start": v(-2.24, -11.87) * mm, "end": v(-12.24, -11.87) * mm});
            skLineSegment(sketch, "E176.MirrorCS", {"start": v(-28.24, 14.13) * mm, "end": v(-38.24, 14.13) * mm});
            skLineSegment(sketch, "E177.MirrorCS", {"start": v(39.76, -47.87) * mm, "end": v(49.76, -47.87) * mm});
            skLineSegment(sketch, "E178.MirrorCS", {"start": v(39.76, 14.13) * mm, "end": v(49.76, 14.13) * mm});
            skLineSegment(sketch, "E179.MirrorCS", {"start": v(-15.24, -24.87) * mm, "end": v(-25.24, -24.87) * mm});
            skLineSegment(sketch, "E180.MirrorCS", {"start": v(39.76, -8.87) * mm, "end": v(49.76, -8.87) * mm});
            skLineSegment(sketch, "E181.MirrorCS", {"start": v(13.76, -50.87) * mm, "end": v(23.76, -50.87) * mm});
            skLineSegment(sketch, "E182.MirrorCS", {"start": v(-41.24, 27.13) * mm, "end": v(-51.24, 27.13) * mm});
            skLineSegment(sketch, "E183.MirrorCS", {"start": v(26.76, 17.13) * mm, "end": v(36.76, 17.13) * mm});
            skLineSegment(sketch, "E184.MirrorCS", {"start": v(0.76, -37.87) * mm, "end": v(0.76, -47.87) * mm});
            skLineSegment(sketch, "E185.MirrorCS", {"start": v(26.76, 1.13) * mm, "end": v(36.76, 1.13) * mm});
            skLineSegment(sketch, "E186.MirrorCS", {"start": v(0.76, -24.87) * mm, "end": v(0.76, -34.87) * mm});
            skLineSegment(sketch, "E187.MirrorCS", {"start": v(49.76, -50.87) * mm, "end": v(49.76, -60.87) * mm});
            skLineSegment(sketch, "E188.MirrorCS", {"start": v(-51.24, -11.87) * mm, "end": v(-51.24, -21.87) * mm});
            skLineSegment(sketch, "E189.MirrorCS", {"start": v(49.76, 14.13) * mm, "end": v(49.76, 4.13) * mm});
            skLineSegment(sketch, "E190.MirrorCS", {"start": v(-25.24, -37.87) * mm, "end": v(-25.24, -47.87) * mm});
            skLineSegment(sketch, "E191.MirrorCS", {"start": v(-38.24, 1.13) * mm, "end": v(-38.24, -8.87) * mm});
            skLineSegment(sketch, "E192.MirrorCS", {"start": v(-38.24, -50.87) * mm, "end": v(-38.24, -60.87) * mm});
            skLineSegment(sketch, "E193.MirrorCS", {"start": v(-12.24, -24.87) * mm, "end": v(-12.24, -34.87) * mm});
            skLineSegment(sketch, "E194.MirrorCS", {"start": v(-15.24, -37.87) * mm, "end": v(-25.24, -37.87) * mm});
            skLineSegment(sketch, "E195.MirrorCS", {"start": v(-2.24, -24.87) * mm, "end": v(-12.24, -24.87) * mm});
            skLineSegment(sketch, "E196.MirrorCS", {"start": v(-41.24, -11.87) * mm, "end": v(-51.24, -11.87) * mm});
            skLineSegment(sketch, "E197.MirrorCS", {"start": v(-28.24, -50.87) * mm, "end": v(-38.24, -50.87) * mm});
            skLineSegment(sketch, "E198.MirrorCS", {"start": v(-28.24, 1.13) * mm, "end": v(-38.24, 1.13) * mm});
            skLineSegment(sketch, "E199.MirrorCS", {"start": v(-2.24, -37.87) * mm, "end": v(-12.24, -37.87) * mm});
            skLineSegment(sketch, "E200.MirrorCS", {"start": v(26.76, -50.87) * mm, "end": v(36.76, -50.87) * mm});
            skLineSegment(sketch, "E201.MirrorCS", {"start": v(39.76, -24.87) * mm, "end": v(39.76, -34.87) * mm});
            skLineSegment(sketch, "E202.MirrorCS", {"start": v(36.76, -24.87) * mm, "end": v(36.76, -34.87) * mm});
            skLineSegment(sketch, "E203.MirrorCS", {"start": v(39.76, -24.87) * mm, "end": v(49.76, -24.87) * mm});
            skLineSegment(sketch, "E204.MirrorCS", {"start": v(26.76, -34.87) * mm, "end": v(36.76, -34.87) * mm});
            skLineSegment(sketch, "E205.MirrorCS", {"start": v(23.76, -24.87) * mm, "end": v(23.76, -34.87) * mm});
            skLineSegment(sketch, "E206.MirrorCS", {"start": v(13.76, 14.13) * mm, "end": v(13.76, 4.13) * mm});
            skLineSegment(sketch, "E207.MirrorCS", {"start": v(-15.24, -47.87) * mm, "end": v(-25.24, -47.87) * mm});
            skLineSegment(sketch, "E208.MirrorCS", {"start": v(-2.24, -34.87) * mm, "end": v(-12.24, -34.87) * mm});
            skLineSegment(sketch, "E209.MirrorCS", {"start": v(26.76, 27.13) * mm, "end": v(26.76, 17.13) * mm});
            skLineSegment(sketch, "E210.MirrorCS", {"start": v(-41.24, -21.87) * mm, "end": v(-51.24, -21.87) * mm});
            skLineSegment(sketch, "E211.MirrorCS", {"start": v(-28.24, -60.87) * mm, "end": v(-38.24, -60.87) * mm});
            skLineSegment(sketch, "E212.MirrorCS", {"start": v(-28.24, -8.87) * mm, "end": v(-38.24, -8.87) * mm});
            skLineSegment(sketch, "E213.MirrorCS", {"start": v(39.76, -11.87) * mm, "end": v(49.76, -11.87) * mm});
            skLineSegment(sketch, "E214.MirrorCS", {"start": v(39.76, 27.13) * mm, "end": v(39.76, 17.13) * mm});
            skLineSegment(sketch, "E215.MirrorCS", {"start": v(13.76, -11.87) * mm, "end": v(23.76, -11.87) * mm});
            skLineSegment(sketch, "E216.MirrorCS", {"start": v(39.76, 27.13) * mm, "end": v(49.76, 27.13) * mm});
            skLineSegment(sketch, "E217.MirrorCS", {"start": v(0.76, -8.87) * mm, "end": v(10.76, -8.87) * mm});
            skLineSegment(sketch, "E218.MirrorCS", {"start": v(36.76, 14.13) * mm, "end": v(36.76, 4.13) * mm});
            skLineSegment(sketch, "E219.MirrorCS", {"start": v(13.76, -37.87) * mm, "end": v(13.76, -47.87) * mm});
            skLineSegment(sketch, "E220.MirrorCS", {"start": v(-15.24, -50.87) * mm, "end": v(-15.24, -60.87) * mm});
            skLineSegment(sketch, "E221.MirrorCS", {"start": v(-2.24, -37.87) * mm, "end": v(-2.24, -47.87) * mm});
            skLineSegment(sketch, "E222.MirrorCS", {"start": v(-15.24, 1.13) * mm, "end": v(-15.24, -8.87) * mm});
            skLineSegment(sketch, "E223.MirrorCS", {"start": v(13.76, 14.13) * mm, "end": v(23.76, 14.13) * mm});
            skLineSegment(sketch, "E224.MirrorCS", {"start": v(-41.24, -24.87) * mm, "end": v(-41.24, -34.87) * mm});
            skLineSegment(sketch, "E225.MirrorCS", {"start": v(-41.24, 27.13) * mm, "end": v(-41.24, 17.13) * mm});
            skLineSegment(sketch, "E226.MirrorCS", {"start": v(-28.24, -11.87) * mm, "end": v(-28.24, -21.87) * mm});
            skLineSegment(sketch, "E227.MirrorCS", {"start": v(0.76, -24.87) * mm, "end": v(10.76, -24.87) * mm});
            skLineSegment(sketch, "E228.MirrorCS", {"start": v(26.76, -11.87) * mm, "end": v(26.76, -21.87) * mm});
            skLineSegment(sketch, "E229.MirrorCS", {"start": v(10.76, 1.13) * mm, "end": v(10.76, -8.87) * mm});
            skLineSegment(sketch, "E230.MirrorCS", {"start": v(0.76, 27.13) * mm, "end": v(10.76, 27.13) * mm});
            skLineSegment(sketch, "E231.MirrorCS", {"start": v(36.76, -37.87) * mm, "end": v(36.76, -47.87) * mm});
            skLineSegment(sketch, "E232.MirrorCS", {"start": v(26.76, -47.87) * mm, "end": v(36.76, -47.87) * mm});
            skLineSegment(sketch, "E233.MirrorCS", {"start": v(-25.24, -50.87) * mm, "end": v(-25.24, -60.87) * mm});
            skLineSegment(sketch, "E234.MirrorCS", {"start": v(-25.24, 1.13) * mm, "end": v(-25.24, -8.87) * mm});
            skLineSegment(sketch, "E235.MirrorCS", {"start": v(-12.24, -37.87) * mm, "end": v(-12.24, -47.87) * mm});
            skLineSegment(sketch, "E236.MirrorCS", {"start": v(13.76, 17.13) * mm, "end": v(23.76, 17.13) * mm});
            skLineSegment(sketch, "E237.MirrorCS", {"start": v(-51.24, -24.87) * mm, "end": v(-51.24, -34.87) * mm});
            skLineSegment(sketch, "E238.MirrorCS", {"start": v(-51.24, 27.13) * mm, "end": v(-51.24, 17.13) * mm});
            skLineSegment(sketch, "E239.MirrorCS", {"start": v(-38.24, -11.87) * mm, "end": v(-38.24, -21.87) * mm});
            skLineSegment(sketch, "E240.MirrorCS", {"start": v(13.76, -37.87) * mm, "end": v(23.76, -37.87) * mm});
            skLineSegment(sketch, "E241.MirrorCS", {"start": v(26.76, -11.87) * mm, "end": v(36.76, -11.87) * mm});
            skLineSegment(sketch, "E242.MirrorCS", {"start": v(0.76, -50.87) * mm, "end": v(10.76, -50.87) * mm});
            skLineSegment(sketch, "E243.MirrorCS", {"start": v(0.76, 17.13) * mm, "end": v(10.76, 17.13) * mm});
            skLineSegment(sketch, "E244.MirrorCS", {"start": v(10.76, -11.87) * mm, "end": v(10.76, -21.87) * mm});
            skLineSegment(sketch, "E245.MirrorCS", {"start": v(26.76, 4.13) * mm, "end": v(36.76, 4.13) * mm});
            skLineSegment(sketch, "E246.MirrorCS", {"start": v(-28.24, -24.87) * mm, "end": v(-28.24, -34.87) * mm});
            skLineSegment(sketch, "E247.MirrorCS", {"start": v(-15.24, -11.87) * mm, "end": v(-15.24, -21.87) * mm});
            skLineSegment(sketch, "E248.MirrorCS", {"start": v(-2.24, -50.87) * mm, "end": v(-2.24, -60.87) * mm});
            skLineSegment(sketch, "E249.MirrorCS", {"start": v(39.76, -37.87) * mm, "end": v(39.76, -47.87) * mm});
            skLineSegment(sketch, "E250.MirrorCS", {"start": v(-41.24, -37.87) * mm, "end": v(-41.24, -47.87) * mm});
            skLineSegment(sketch, "E251.MirrorCS", {"start": v(26.76, -21.87) * mm, "end": v(36.76, -21.87) * mm});
            skLineSegment(sketch, "E252.MirrorCS", {"start": v(-41.24, 14.13) * mm, "end": v(-41.24, 4.13) * mm});
            skLineSegment(sketch, "E253.MirrorCS", {"start": v(0.76, -21.87) * mm, "end": v(10.76, -21.87) * mm});
            skLineSegment(sketch, "E254.MirrorCS", {"start": v(49.76, -11.87) * mm, "end": v(49.76, -21.87) * mm});
            skLineSegment(sketch, "E255.MirrorCS", {"start": v(23.76, 1.13) * mm, "end": v(23.76, -8.87) * mm});
            skLineSegment(sketch, "E256.MirrorCS", {"start": v(0.76, -50.87) * mm, "end": v(0.76, -60.87) * mm});
            skLineSegment(sketch, "E257.MirrorCS", {"start": v(13.76, 27.13) * mm, "end": v(13.76, 17.13) * mm});
            skLineSegment(sketch, "E258.MirrorCS", {"start": v(-15.24, -60.87) * mm, "end": v(-25.24, -60.87) * mm});
            skLineSegment(sketch, "E259.MirrorCS", {"start": v(-15.24, -8.87) * mm, "end": v(-25.24, -8.87) * mm});
            skLineSegment(sketch, "E260.MirrorCS", {"start": v(-2.24, -47.87) * mm, "end": v(-12.24, -47.87) * mm});
            skLineSegment(sketch, "E261.MirrorCS", {"start": v(23.76, 27.13) * mm, "end": v(23.76, 17.13) * mm});
            skLineSegment(sketch, "E262.MirrorCS", {"start": v(-41.24, -34.87) * mm, "end": v(-51.24, -34.87) * mm});
            skLineSegment(sketch, "E263.MirrorCS", {"start": v(-41.24, 17.13) * mm, "end": v(-51.24, 17.13) * mm});
            skLineSegment(sketch, "E264.MirrorCS", {"start": v(-28.24, -21.87) * mm, "end": v(-38.24, -21.87) * mm});
            skLineSegment(sketch, "E265.MirrorCS", {"start": v(36.76, -50.87) * mm, "end": v(36.76, -60.87) * mm});
            skLineSegment(sketch, "E266.MirrorCS", {"start": v(10.76, -37.87) * mm, "end": v(10.76, -47.87) * mm});
            skLineSegment(sketch, "E267.MirrorCS", {"start": v(36.76, 27.13) * mm, "end": v(36.76, 17.13) * mm});
            skLineSegment(sketch, "E268.MirrorCS", {"start": v(0.76, 14.13) * mm, "end": v(0.76, 4.13) * mm});
            skLineSegment(sketch, "E269.MirrorCS", {"start": v(39.76, -50.87) * mm, "end": v(39.76, -60.87) * mm});
            skLineSegment(sketch, "E270.MirrorCS", {"start": v(39.76, -60.87) * mm, "end": v(49.76, -60.87) * mm});
            skLineSegment(sketch, "E271.MirrorCS", {"start": v(-38.24, -24.87) * mm, "end": v(-38.24, -34.87) * mm});
            skLineSegment(sketch, "E272.MirrorCS", {"start": v(-38.24, 27.13) * mm, "end": v(-38.24, 17.13) * mm});
            skLineSegment(sketch, "E273.MirrorCS", {"start": v(-25.24, -11.87) * mm, "end": v(-25.24, -21.87) * mm});
            skLineSegment(sketch, "E274.MirrorCS", {"start": v(-12.24, -50.87) * mm, "end": v(-12.24, -60.87) * mm});
            skLineSegment(sketch, "E275.MirrorCS", {"start": v(39.76, 14.13) * mm, "end": v(39.76, 4.13) * mm});
            skLineSegment(sketch, "E276.MirrorCS", {"start": v(13.76, -60.87) * mm, "end": v(23.76, -60.87) * mm});
            skLineSegment(sketch, "E277.MirrorCS", {"start": v(-51.24, -37.87) * mm, "end": v(-51.24, -47.87) * mm});
            skLineSegment(sketch, "E278.MirrorCS", {"start": v(-51.24, 14.13) * mm, "end": v(-51.24, 4.13) * mm});
            skLineSegment(sketch, "E279.MirrorCS", {"start": v(13.76, -34.87) * mm, "end": v(23.76, -34.87) * mm});
            skLineSegment(sketch, "E280.MirrorCS", {"start": v(10.76, 27.13) * mm, "end": v(10.76, 14.13) * mm, "construction": true});
            skLineSegment(sketch, "E281.MirrorCS", {"start": v(23.76, -50.87) * mm, "end": v(23.76, -60.87) * mm});
            skLineSegment(sketch, "E282.MirrorCS", {"start": v(13.76, 1.13) * mm, "end": v(23.76, 1.13) * mm});
            skLineSegment(sketch, "E283.MirrorCS", {"start": v(13.76, -24.87) * mm, "end": v(13.76, -34.87) * mm});
            skLineSegment(sketch, "E284.MirrorCS", {"start": v(-28.24, -24.87) * mm, "end": v(-38.24, -24.87) * mm});
            skLineSegment(sketch, "E285.MirrorCS", {"start": v(-28.24, 27.13) * mm, "end": v(-38.24, 27.13) * mm});
            skLineSegment(sketch, "E286.MirrorCS", {"start": v(-15.24, -11.87) * mm, "end": v(-25.24, -11.87) * mm});
            skLineSegment(sketch, "E287.MirrorCS", {"start": v(-2.24, -50.87) * mm, "end": v(-12.24, -50.87) * mm});
            skLineSegment(sketch, "E288.MirrorCS", {"start": v(0.76, 1.13) * mm, "end": v(0.76, -8.87) * mm});
            skLineSegment(sketch, "E289.MirrorCS", {"start": v(13.76, -8.87) * mm, "end": v(23.76, -8.87) * mm});
            skLineSegment(sketch, "E290.MirrorCS", {"start": v(-41.24, -37.87) * mm, "end": v(-51.24, -37.87) * mm});
            skLineSegment(sketch, "E291.MirrorCS", {"start": v(-41.24, 14.13) * mm, "end": v(-51.24, 14.13) * mm});
            skLineSegment(sketch, "E292.MirrorCS", {"start": v(39.76, 1.13) * mm, "end": v(49.76, 1.13) * mm});
            skLineSegment(sketch, "E293.MirrorCS", {"start": v(10.76, -24.87) * mm, "end": v(10.76, -34.87) * mm});
            skLineSegment(sketch, "E294.MirrorCS", {"start": v(36.76, -11.87) * mm, "end": v(36.76, -21.87) * mm});
            skLineSegment(sketch, "E295.MirrorCS", {"start": v(13.76, -11.87) * mm, "end": v(13.76, -21.87) * mm});
            skLineSegment(sketch, "E296.MirrorCS", {"start": v(26.76, 14.13) * mm, "end": v(26.76, 4.13) * mm});
            skLineSegment(sketch, "E297.MirrorCS", {"start": v(-2.24, 1.13) * mm, "end": v(-2.24, -8.87) * mm});
            skLineSegment(sketch, "E298.MirrorCS", {"start": v(-12.24, 1.13) * mm, "end": v(-12.24, -8.87) * mm});
            skLineSegment(sketch, "E299.MirrorCS", {"start": v(-2.24, 1.13) * mm, "end": v(-12.24, 1.13) * mm});
            skLineSegment(sketch, "E300.MirrorCS", {"start": v(-2.24, 27.13) * mm, "end": v(-12.24, 27.13) * mm});
            skLineSegment(sketch, "E301.MirrorCS", {"start": v(-2.24, 14.13) * mm, "end": v(-2.24, 4.13) * mm});
            skLineSegment(sketch, "E302.MirrorCS", {"start": v(-12.24, 14.13) * mm, "end": v(-12.24, 4.13) * mm});
            skLineSegment(sketch, "E303.MirrorCS", {"start": v(-2.24, 4.13) * mm, "end": v(-12.24, 4.13) * mm});
            skLineSegment(sketch, "E304.MirrorCS", {"start": v(26.76, -24.87) * mm, "end": v(26.76, -34.87) * mm});
            skLineSegment(sketch, "E305.MirrorCS", {"start": v(0.76, -47.87) * mm, "end": v(10.76, -47.87) * mm});
            skLineSegment(sketch, "E306.MirrorCS", {"start": v(-41.24, -47.87) * mm, "end": v(-51.24, -47.87) * mm});
            skLineSegment(sketch, "E307.MirrorCS", {"start": v(-41.24, 4.13) * mm, "end": v(-51.24, 4.13) * mm});
            skLineSegment(sketch, "E308.MirrorCS", {"start": v(39.76, -50.87) * mm, "end": v(49.76, -50.87) * mm});
            skLineSegment(sketch, "E309.MirrorCS", {"start": v(23.76, 14.13) * mm, "end": v(23.76, 4.13) * mm});
            skLineSegment(sketch, "E310.MirrorCS", {"start": v(26.76, -8.87) * mm, "end": v(36.76, -8.87) * mm});
            skLineSegment(sketch, "E311.MirrorCS", {"start": v(26.76, 27.13) * mm, "end": v(36.76, 27.13) * mm});
            skLineSegment(sketch, "E312.MirrorCS", {"start": v(26.76, -37.87) * mm, "end": v(26.76, -47.87) * mm});
            skLineSegment(sketch, "E313.MirrorCS", {"start": v(-2.24, -8.87) * mm, "end": v(-12.24, -8.87) * mm});
            skLineSegment(sketch, "E314.MirrorCS", {"start": v(-28.24, -34.87) * mm, "end": v(-38.24, -34.87) * mm});
            skLineSegment(sketch, "E315.MirrorCS", {"start": v(-28.24, 17.13) * mm, "end": v(-38.24, 17.13) * mm});
            skLineSegment(sketch, "E316.MirrorCS", {"start": v(-15.24, -21.87) * mm, "end": v(-25.24, -21.87) * mm});
            skLineSegment(sketch, "E317.MirrorCS", {"start": v(-2.24, -60.87) * mm, "end": v(-12.24, -60.87) * mm});
            skLineSegment(sketch, "E318.MirrorCS", {"start": v(13.76, -24.87) * mm, "end": v(23.76, -24.87) * mm});
            skLineSegment(sketch, "E319.MirrorCS", {"start": v(23.76, -37.87) * mm, "end": v(23.76, -47.87) * mm});
            skLineSegment(sketch, "E320.MirrorCS", {"start": v(26.76, -60.87) * mm, "end": v(36.76, -60.87) * mm});
            skLineSegment(sketch, "E321.MirrorCS", {"start": v(10.76, -50.87) * mm, "end": v(10.76, -60.87) * mm});
            skLineSegment(sketch, "E322.MirrorCS", {"start": v(0.76, -11.87) * mm, "end": v(0.76, -21.87) * mm});
            skLineSegment(sketch, "E323.MirrorCS", {"start": v(-2.24, -11.87) * mm, "end": v(-2.24, -21.87) * mm});
            skLineSegment(sketch, "E324.MirrorCS", {"start": v(-28.24, -37.87) * mm, "end": v(-28.24, -47.87) * mm});
            skLineSegment(sketch, "E325.MirrorCS", {"start": v(-28.24, 14.13) * mm, "end": v(-28.24, 4.13) * mm});
            skLineSegment(sketch, "E326.MirrorCS", {"start": v(-15.24, -24.87) * mm, "end": v(-15.24, -34.87) * mm});
            skLineSegment(sketch, "E327.MirrorCS", {"start": v(-15.24, 27.13) * mm, "end": v(-15.24, 17.13) * mm});
            skLineSegment(sketch, "E328.MirrorCS", {"start": v(49.76, -37.87) * mm, "end": v(49.76, -47.87) * mm});
            skLineSegment(sketch, "E329.MirrorCS", {"start": v(39.76, -34.87) * mm, "end": v(49.76, -34.87) * mm});
            skLineSegment(sketch, "E330.MirrorCS", {"start": v(-41.24, -50.87) * mm, "end": v(-41.24, -60.87) * mm});
            skLineSegment(sketch, "E331.MirrorCS", {"start": v(-41.24, 1.13) * mm, "end": v(-41.24, -8.87) * mm});
            skLineSegment(sketch, "E332.MirrorCS", {"start": v(39.76, 4.13) * mm, "end": v(49.76, 4.13) * mm});
            skLineSegment(sketch, "E333.MirrorCS", {"start": v(-12.24, -11.87) * mm, "end": v(-12.24, -21.87) * mm});
            skLineSegment(sketch, "E334.MirrorCS", {"start": v(-38.24, -37.87) * mm, "end": v(-38.24, -47.87) * mm});
            skLineSegment(sketch, "E335.MirrorCS", {"start": v(-38.24, 14.13) * mm, "end": v(-38.24, 4.13) * mm});
            skLineSegment(sketch, "E336.MirrorCS", {"start": v(-25.24, -24.87) * mm, "end": v(-25.24, -34.87) * mm});
            skLineSegment(sketch, "E337.MirrorCS", {"start": v(39.76, -37.87) * mm, "end": v(49.76, -37.87) * mm});
            skLineSegment(sketch, "E338.MirrorCS", {"start": v(39.76, 17.13) * mm, "end": v(49.76, 17.13) * mm});
            skLineSegment(sketch, "E339.MirrorCS", {"start": v(-51.24, -50.87) * mm, "end": v(-51.24, -60.87) * mm});
            skLineSegment(sketch, "E340.MirrorCS", {"start": v(-51.24, 1.13) * mm, "end": v(-51.24, -8.87) * mm});
            skLineSegment(sketch, "E341.MirrorCS", {"start": v(26.76, 14.13) * mm, "end": v(36.76, 14.13) * mm});
            skLineSegment(sketch, "E342.MirrorCS", {"start": v(26.76, 1.13) * mm, "end": v(26.76, -8.87) * mm});
            skLineSegment(sketch, "E343.MirrorCS", {"start": v(39.76, -21.87) * mm, "end": v(49.76, -21.87) * mm});
            skLineSegment(sketch, "E344.MirrorCS", {"start": v(49.76, -24.87) * mm, "end": v(49.76, -34.87) * mm});
            skSolve(sketch);
        }
        {
            var Q0;
            Q0=makeQuery(id+"F0.imprint","IMPRINT",FACE,{"disambiguationData":[TD([[makeQuery(id+"F0.imprint","IMPRINT",EDGE,{"derivedFrom":sQuery(id+"F0.wireOp",EDGE,"E0.bottom")}),-1.0]])]});
            extrude(context, id + "F1", {"entities" : qUnion([Q0]), "depth" : 2.5 * mm});
        }
        {
            var Q0;
            Q0=makeQuery(id+"F1.opExtrude","CAP_FACE",FACE,{"disambiguationData":[OSD([sQuery(id+"F0.wireOp",EDGE,"E0.bottom"),sQuery(id+"F0.wireOp",EDGE,"E0.top"),sQuery(id+"F0.wireOp",EDGE,"E0.left"),sQuery(id+"F0.wireOp",EDGE,"E0.right"),sQuery(id+"F0.wireOp",EDGE,"hA2XBF1b-iAit-YRYK-yzPq-8CkU7Wwz4iKJ.bottom"),sQuery(id+"F0.wireOp",EDGE,"hA2XBF1b-iAit-YRYK-yzPq-8CkU7Wwz4iKJ.top"),sQuery(id+"F0.wireOp",EDGE,"hA2XBF1b-iAit-YRYK-yzPq-8CkU7Wwz4iKJ.left"),sQuery(id+"F0.wireOp",EDGE,"hA2XBF1b-iAit-YRYK-yzPq-8CkU7Wwz4iKJ.right"),sQuery(id+"F0.wireOp",EDGE,"c2419bcc-613f-4a5b-81a1-cea1710afb35.0.1.0"),sQuery(id+"F0.wireOp",EDGE,"c2419bcc-613f-4a5b-81a1-cea1710afb35.0.1.1"),sQuery(id+"F0.wireOp",EDGE,"c2419bcc-613f-4a5b-81a1-cea1710afb35.0.1.2"),sQuery(id+"F0.wireOp",EDGE,"c2419bcc-613f-4a5b-81a1-cea1710afb35.0.1.3"),sQuery(id+"F0.wireOp",EDGE,"c2419bcc-613f-4a5b-81a1-cea1710afb35.0.2.0"),sQuery(id+"F0.wireOp",EDGE,"c2419bcc-613f-4a5b-81a1-cea1710afb35.0.2.1"),sQuery(id+"F0.wireOp",EDGE,"c2419bcc-613f-4a5b-81a1-cea1710afb35.0.2.2"),sQuery(id+"F0.wireOp",EDGE,"c2419bcc-613f-4a5b-81a1-cea1710afb35.0.2.3"),sQuery(id+"F0.wireOp",EDGE,"c2419bcc-613f-4a5b-81a1-cea1710afb35.0.3.0"),sQuery(id+"F0.wireOp",EDGE,"c2419bcc-613f-4a5b-81a1-cea1710afb35.0.3.1"),sQuery(id+"F0.wireOp",EDGE,"c2419bcc-613f-4a5b-81a1-cea1710afb35.0.3.2"),sQuery(id+"F0.wireOp",EDGE,"c2419bcc-613f-4a5b-81a1-cea1710afb35.0.3.3"),sQuery(id+"F0.wireOp",EDGE,"c2419bcc-613f-4a5b-81a1-cea1710afb35.0.4.0"),sQuery(id+"F0.wireOp",EDGE,"c2419bcc-613f-4a5b-81a1-cea1710afb35.0.4.1"),sQuery(id+"F0.wireOp",EDGE,"c2419bcc-613f-4a5b-81a1-cea1710afb35.0.4.2"),sQuery(id+"F0.wireOp",EDGE,"c2419bcc-613f-4a5b-81a1-cea1710afb35.0.4.3"),sQuery(id+"F0.wireOp",EDGE,"c2419bcc-613f-4a5b-81a1-cea1710afb35.0.5.0"),sQuery(id+"F0.wireOp",EDGE,"c2419bcc-613f-4a5b-81a1-cea1710afb35.0.5.1"),sQuery(id+"F0.wireOp",EDGE,"c2419bcc-613f-4a5b-81a1-cea1710afb35.0.5.2"),sQuery(id+"F0.wireOp",EDGE,"c2419bcc-613f-4a5b-81a1-cea1710afb35.0.5.3"),sQuery(id+"F0.wireOp",EDGE,"c2419bcc-613f-4a5b-81a1-cea1710afb35.0.6.0"),sQuery(id+"F0.wireOp",EDGE,"c2419bcc-613f-4a5b-81a1-cea1710afb35.0.6.1"),sQuery(id+"F0.wireOp",EDGE,"c2419bcc-613f-4a5b-81a1-cea1710afb35.0.6.2"),sQuery(id+"F0.wireOp",EDGE,"c2419bcc-613f-4a5b-81a1-cea1710afb35.0.6.3"),sQuery(id+"F0.wireOp",EDGE,"c2419bcc-613f-4a5b-81a1-cea1710afb35.0.7.0"),sQuery(id+"F0.wireOp",EDGE,"c2419bcc-613f-4a5b-81a1-cea1710afb35.0.7.1"),sQuery(id+"F0.wireOp",EDGE,"c2419bcc-613f-4a5b-81a1-cea1710afb35.0.7.2"),sQuery(id+"F0.wireOp",EDGE,"c2419bcc-613f-4a5b-81a1-cea1710afb35.0.7.3"),sQuery(id+"F0.wireOp",EDGE,"c2419bcc-613f-4a5b-81a1-cea1710afb35.0.8.0"),sQuery(id+"F0.wireOp",EDGE,"c2419bcc-613f-4a5b-81a1-cea1710afb35.0.8.1"),sQuery(id+"F0.wireOp",EDGE,"c2419bcc-613f-4a5b-81a1-cea1710afb35.0.8.2"),sQuery(id+"F0.wireOp",EDGE,"c2419bcc-613f-4a5b-81a1-cea1710afb35.0.8.3"),sQuery(id+"F0.wireOp",EDGE,"c2419bcc-613f-4a5b-81a1-cea1710afb35.0.9.0"),sQuery(id+"F0.wireOp",EDGE,"c2419bcc-613f-4a5b-81a1-cea1710afb35.0.9.1"),sQuery(id+"F0.wireOp",EDGE,"c2419bcc-613f-4a5b-81a1-cea1710afb35.0.9.2"),sQuery(id+"F0.wireOp",EDGE,"c2419bcc-613f-4a5b-81a1-cea1710afb35.0.9.3"),sQuery(id+"F0.wireOp",EDGE,"c2419bcc-613f-4a5b-81a1-cea1710afb35.0.10.0"),sQuery(id+"F0.wireOp",EDGE,"c2419bcc-613f-4a5b-81a1-cea1710afb35.0.10.1"),sQuery(id+"F0.wireOp",EDGE,"c2419bcc-613f-4a5b-81a1-cea1710afb35.0.10.2"),sQuery(id+"F0.wireOp",EDGE,"c2419bcc-613f-4a5b-81a1-cea1710afb35.0.10.3"),sQuery(id+"F0.wireOp",EDGE,"c2419bcc-613f-4a5b-81a1-cea1710afb35.0.11.0"),sQuery(id+"F0.wireOp",EDGE,"c2419bcc-613f-4a5b-81a1-cea1710afb35.0.11.1"),sQuery(id+"F0.wireOp",EDGE,"c2419bcc-613f-4a5b-81a1-cea1710afb35.0.11.2"),sQuery(id+"F0.wireOp",EDGE,"c2419bcc-613f-4a5b-81a1-cea1710afb35.0.11.3"),sQuery(id+"F0.wireOp",EDGE,"c2419bcc-613f-4a5b-81a1-cea1710afb35.0.12.0"),sQuery(id+"F0.wireOp",EDGE,"c2419bcc-613f-4a5b-81a1-cea1710afb35.0.12.1"),sQuery(id+"F0.wireOp",EDGE,"c2419bcc-613f-4a5b-81a1-cea1710afb35.0.12.2"),sQuery(id+"F0.wireOp",EDGE,"c2419bcc-613f-4a5b-81a1-cea1710afb35.0.12.3"),sQuery(id+"F0.wireOp",EDGE,"c2419bcc-613f-4a5b-81a1-cea1710afb35.0.13.0"),sQuery(id+"F0.wireOp",EDGE,"c2419bcc-613f-4a5b-81a1-cea1710afb35.0.13.1"),sQuery(id+"F0.wireOp",EDGE,"c2419bcc-613f-4a5b-81a1-cea1710afb35.0.13.2"),sQuery(id+"F0.wireOp",EDGE,"c2419bcc-613f-4a5b-81a1-cea1710afb35.0.13.3"),sQuery(id+"F0.wireOp",EDGE,"c2419bcc-613f-4a5b-81a1-cea1710afb35.1.0.0"),sQuery(id+"F0.wireOp",EDGE,"c2419bcc-613f-4a5b-81a1-cea1710afb35.1.0.1"),sQuery(id+"F0.wireOp",EDGE,"c2419bcc-613f-4a5b-81a1-cea1710afb35.1.0.2"),sQuery(id+"F0.wireOp",EDGE,"c2419bcc-613f-4a5b-81a1-cea1710afb35.1.0.3"),sQuery(id+"F0.wireOp",EDGE,"c2419bcc-613f-4a5b-81a1-cea1710afb35.1.1.0"),sQuery(id+"F0.wireOp",EDGE,"c2419bcc-613f-4a5b-81a1-cea1710afb35.1.1.1"),sQuery(id+"F0.wireOp",EDGE,"c2419bcc-613f-4a5b-81a1-cea1710afb35.1.1.2"),sQuery(id+"F0.wireOp",EDGE,"c2419bcc-613f-4a5b-81a1-cea1710afb35.1.1.3"),sQuery(id+"F0.wireOp",EDGE,"c2419bcc-613f-4a5b-81a1-cea1710afb35.1.2.0"),sQuery(id+"F0.wireOp",EDGE,"c2419bcc-613f-4a5b-81a1-cea1710afb35.1.2.1"),sQuery(id+"F0.wireOp",EDGE,"c2419bcc-613f-4a5b-81a1-cea1710afb35.1.2.2"),sQuery(id+"F0.wireOp",EDGE,"c2419bcc-613f-4a5b-81a1-cea1710afb35.1.2.3"),sQuery(id+"F0.wireOp",EDGE,"c2419bcc-613f-4a5b-81a1-cea1710afb35.1.3.0"),sQuery(id+"F0.wireOp",EDGE,"c2419bcc-613f-4a5b-81a1-cea1710afb35.1.3.1"),sQuery(id+"F0.wireOp",EDGE,"c2419bcc-613f-4a5b-81a1-cea1710afb35.1.3.2"),sQuery(id+"F0.wireOp",EDGE,"c2419bcc-613f-4a5b-81a1-cea1710afb35.1.3.3"),sQuery(id+"F0.wireOp",EDGE,"c2419bcc-613f-4a5b-81a1-cea1710afb35.1.4.0"),sQuery(id+"F0.wireOp",EDGE,"c2419bcc-613f-4a5b-81a1-cea1710afb35.1.4.1"),sQuery(id+"F0.wireOp",EDGE,"c2419bcc-613f-4a5b-81a1-cea1710afb35.1.4.2"),sQuery(id+"F0.wireOp",EDGE,"c2419bcc-613f-4a5b-81a1-cea1710afb35.1.4.3"),sQuery(id+"F0.wireOp",EDGE,"c2419bcc-613f-4a5b-81a1-cea1710afb35.1.5.0"),sQuery(id+"F0.wireOp",EDGE,"c2419bcc-613f-4a5b-81a1-cea1710afb35.1.5.1"),sQuery(id+"F0.wireOp",EDGE,"c2419bcc-613f-4a5b-81a1-cea1710afb35.1.5.2"),sQuery(id+"F0.wireOp",EDGE,"c2419bcc-613f-4a5b-81a1-cea1710afb35.1.5.3"),sQuery(id+"F0.wireOp",EDGE,"c2419bcc-613f-4a5b-81a1-cea1710afb35.1.6.0"),sQuery(id+"F0.wireOp",EDGE,"c2419bcc-613f-4a5b-81a1-cea1710afb35.1.6.1"),sQuery(id+"F0.wireOp",EDGE,"c2419bcc-613f-4a5b-81a1-cea1710afb35.1.6.2"),sQuery(id+"F0.wireOp",EDGE,"c2419bcc-613f-4a5b-81a1-cea1710afb35.1.6.3"),sQuery(id+"F0.wireOp",EDGE,"c2419bcc-613f-4a5b-81a1-cea1710afb35.1.7.0"),sQuery(id+"F0.wireOp",EDGE,"c2419bcc-613f-4a5b-81a1-cea1710afb35.1.7.1"),sQuery(id+"F0.wireOp",EDGE,"c2419bcc-613f-4a5b-81a1-cea1710afb35.1.7.2"),sQuery(id+"F0.wireOp",EDGE,"c2419bcc-613f-4a5b-81a1-cea1710afb35.1.7.3"),sQuery(id+"F0.wireOp",EDGE,"c2419bcc-613f-4a5b-81a1-cea1710afb35.1.8.0"),sQuery(id+"F0.wireOp",EDGE,"c2419bcc-613f-4a5b-81a1-cea1710afb35.1.8.1"),sQuery(id+"F0.wireOp",EDGE,"c2419bcc-613f-4a5b-81a1-cea1710afb35.1.8.2"),sQuery(id+"F0.wireOp",EDGE,"c2419bcc-613f-4a5b-81a1-cea1710afb35.1.8.3"),sQuery(id+"F0.wireOp",EDGE,"c2419bcc-613f-4a5b-81a1-cea1710afb35.1.9.0"),sQuery(id+"F0.wireOp",EDGE,"c2419bcc-613f-4a5b-81a1-cea1710afb35.1.9.1"),sQuery(id+"F0.wireOp",EDGE,"c2419bcc-613f-4a5b-81a1-cea1710afb35.1.9.2"),sQuery(id+"F0.wireOp",EDGE,"c2419bcc-613f-4a5b-81a1-cea1710afb35.1.9.3"),sQuery(id+"F0.wireOp",EDGE,"c2419bcc-613f-4a5b-81a1-cea1710afb35.1.10.0"),sQuery(id+"F0.wireOp",EDGE,"c2419bcc-613f-4a5b-81a1-cea1710afb35.1.10.1"),sQuery(id+"F0.wireOp",EDGE,"c2419bcc-613f-4a5b-81a1-cea1710afb35.1.10.2"),sQuery(id+"F0.wireOp",EDGE,"c2419bcc-613f-4a5b-81a1-cea1710afb35.1.10.3"),sQuery(id+"F0.wireOp",EDGE,"c2419bcc-613f-4a5b-81a1-cea1710afb35.1.11.0"),sQuery(id+"F0.wireOp",EDGE,"c2419bcc-613f-4a5b-81a1-cea1710afb35.1.11.1"),sQuery(id+"F0.wireOp",EDGE,"c2419bcc-613f-4a5b-81a1-cea1710afb35.1.11.2"),sQuery(id+"F0.wireOp",EDGE,"c2419bcc-613f-4a5b-81a1-cea1710afb35.1.11.3"),sQuery(id+"F0.wireOp",EDGE,"c2419bcc-613f-4a5b-81a1-cea1710afb35.1.12.0"),sQuery(id+"F0.wireOp",EDGE,"c2419bcc-613f-4a5b-81a1-cea1710afb35.1.12.1"),sQuery(id+"F0.wireOp",EDGE,"c2419bcc-613f-4a5b-81a1-cea1710afb35.1.12.2"),sQuery(id+"F0.wireOp",EDGE,"c2419bcc-613f-4a5b-81a1-cea1710afb35.1.12.3"),sQuery(id+"F0.wireOp",EDGE,"c2419bcc-613f-4a5b-81a1-cea1710afb35.1.13.0"),sQuery(id+"F0.wireOp",EDGE,"c2419bcc-613f-4a5b-81a1-cea1710afb35.1.13.1"),sQuery(id+"F0.wireOp",EDGE,"c2419bcc-613f-4a5b-81a1-cea1710afb35.1.13.2"),sQuery(id+"F0.wireOp",EDGE,"c2419bcc-613f-4a5b-81a1-cea1710afb35.1.13.3"),sQuery(id+"F0.wireOp",EDGE,"c2419bcc-613f-4a5b-81a1-cea1710afb35.2.0.0"),sQuery(id+"F0.wireOp",EDGE,"c2419bcc-613f-4a5b-81a1-cea1710afb35.2.0.1"),sQuery(id+"F0.wireOp",EDGE,"c2419bcc-613f-4a5b-81a1-cea1710afb35.2.0.2"),sQuery(id+"F0.wireOp",EDGE,"c2419bcc-613f-4a5b-81a1-cea1710afb35.2.0.3"),sQuery(id+"F0.wireOp",EDGE,"c2419bcc-613f-4a5b-81a1-cea1710afb35.2.1.0"),sQuery(id+"F0.wireOp",EDGE,"c2419bcc-613f-4a5b-81a1-cea1710afb35.2.1.1"),sQuery(id+"F0.wireOp",EDGE,"c2419bcc-613f-4a5b-81a1-cea1710afb35.2.1.2"),sQuery(id+"F0.wireOp",EDGE,"c2419bcc-613f-4a5b-81a1-cea1710afb35.2.1.3"),sQuery(id+"F0.wireOp",EDGE,"c2419bcc-613f-4a5b-81a1-cea1710afb35.2.2.0"),sQuery(id+"F0.wireOp",EDGE,"c2419bcc-613f-4a5b-81a1-cea1710afb35.2.2.1"),sQuery(id+"F0.wireOp",EDGE,"c2419bcc-613f-4a5b-81a1-cea1710afb35.2.2.2"),sQuery(id+"F0.wireOp",EDGE,"c2419bcc-613f-4a5b-81a1-cea1710afb35.2.2.3"),sQuery(id+"F0.wireOp",EDGE,"c2419bcc-613f-4a5b-81a1-cea1710afb35.2.3.0"),sQuery(id+"F0.wireOp",EDGE,"c2419bcc-613f-4a5b-81a1-cea1710afb35.2.3.1"),sQuery(id+"F0.wireOp",EDGE,"c2419bcc-613f-4a5b-81a1-cea1710afb35.2.3.2"),sQuery(id+"F0.wireOp",EDGE,"c2419bcc-613f-4a5b-81a1-cea1710afb35.2.3.3"),sQuery(id+"F0.wireOp",EDGE,"c2419bcc-613f-4a5b-81a1-cea1710afb35.2.4.0"),sQuery(id+"F0.wireOp",EDGE,"c2419bcc-613f-4a5b-81a1-cea1710afb35.2.4.1"),sQuery(id+"F0.wireOp",EDGE,"c2419bcc-613f-4a5b-81a1-cea1710afb35.2.4.2"),sQuery(id+"F0.wireOp",EDGE,"c2419bcc-613f-4a5b-81a1-cea1710afb35.2.4.3"),sQuery(id+"F0.wireOp",EDGE,"c2419bcc-613f-4a5b-81a1-cea1710afb35.2.5.0"),sQuery(id+"F0.wireOp",EDGE,"c2419bcc-613f-4a5b-81a1-cea1710afb35.2.5.1"),sQuery(id+"F0.wireOp",EDGE,"c2419bcc-613f-4a5b-81a1-cea1710afb35.2.5.2"),sQuery(id+"F0.wireOp",EDGE,"c2419bcc-613f-4a5b-81a1-cea1710afb35.2.5.3"),sQuery(id+"F0.wireOp",EDGE,"c2419bcc-613f-4a5b-81a1-cea1710afb35.2.6.0"),sQuery(id+"F0.wireOp",EDGE,"c2419bcc-613f-4a5b-81a1-cea1710afb35.2.6.1"),sQuery(id+"F0.wireOp",EDGE,"c2419bcc-613f-4a5b-81a1-cea1710afb35.2.6.2"),sQuery(id+"F0.wireOp",EDGE,"c2419bcc-613f-4a5b-81a1-cea1710afb35.2.6.3"),sQuery(id+"F0.wireOp",EDGE,"c2419bcc-613f-4a5b-81a1-cea1710afb35.2.7.0"),sQuery(id+"F0.wireOp",EDGE,"c2419bcc-613f-4a5b-81a1-cea1710afb35.2.7.1"),sQuery(id+"F0.wireOp",EDGE,"c2419bcc-613f-4a5b-81a1-cea1710afb35.2.7.2"),sQuery(id+"F0.wireOp",EDGE,"c2419bcc-613f-4a5b-81a1-cea1710afb35.2.7.3"),sQuery(id+"F0.wireOp",EDGE,"c2419bcc-613f-4a5b-81a1-cea1710afb35.2.8.0"),sQuery(id+"F0.wireOp",EDGE,"c2419bcc-613f-4a5b-81a1-cea1710afb35.2.8.1"),sQuery(id+"F0.wireOp",EDGE,"c2419bcc-613f-4a5b-81a1-cea1710afb35.2.8.2"),sQuery(id+"F0.wireOp",EDGE,"c2419bcc-613f-4a5b-81a1-cea1710afb35.2.8.3"),sQuery(id+"F0.wireOp",EDGE,"c2419bcc-613f-4a5b-81a1-cea1710afb35.2.9.0"),sQuery(id+"F0.wireOp",EDGE,"c2419bcc-613f-4a5b-81a1-cea1710afb35.2.9.1"),sQuery(id+"F0.wireOp",EDGE,"c2419bcc-613f-4a5b-81a1-cea1710afb35.2.9.2"),sQuery(id+"F0.wireOp",EDGE,"c2419bcc-613f-4a5b-81a1-cea1710afb35.2.9.3"),sQuery(id+"F0.wireOp",EDGE,"c2419bcc-613f-4a5b-81a1-cea1710afb35.2.10.0"),sQuery(id+"F0.wireOp",EDGE,"c2419bcc-613f-4a5b-81a1-cea1710afb35.2.10.1"),sQuery(id+"F0.wireOp",EDGE,"c2419bcc-613f-4a5b-81a1-cea1710afb35.2.10.2"),sQuery(id+"F0.wireOp",EDGE,"c2419bcc-613f-4a5b-81a1-cea1710afb35.2.10.3"),sQuery(id+"F0.wireOp",EDGE,"c2419bcc-613f-4a5b-81a1-cea1710afb35.2.11.0"),sQuery(id+"F0.wireOp",EDGE,"c2419bcc-613f-4a5b-81a1-cea1710afb35.2.11.1"),sQuery(id+"F0.wireOp",EDGE,"c2419bcc-613f-4a5b-81a1-cea1710afb35.2.11.2"),sQuery(id+"F0.wireOp",EDGE,"c2419bcc-613f-4a5b-81a1-cea1710afb35.2.11.3"),sQuery(id+"F0.wireOp",EDGE,"c2419bcc-613f-4a5b-81a1-cea1710afb35.2.12.0"),sQuery(id+"F0.wireOp",EDGE,"c2419bcc-613f-4a5b-81a1-cea1710afb35.2.12.1"),sQuery(id+"F0.wireOp",EDGE,"c2419bcc-613f-4a5b-81a1-cea1710afb35.2.12.2"),sQuery(id+"F0.wireOp",EDGE,"c2419bcc-613f-4a5b-81a1-cea1710afb35.2.12.3"),sQuery(id+"F0.wireOp",EDGE,"c2419bcc-613f-4a5b-81a1-cea1710afb35.2.13.0"),sQuery(id+"F0.wireOp",EDGE,"c2419bcc-613f-4a5b-81a1-cea1710afb35.2.13.1"),sQuery(id+"F0.wireOp",EDGE,"c2419bcc-613f-4a5b-81a1-cea1710afb35.2.13.2"),sQuery(id+"F0.wireOp",EDGE,"c2419bcc-613f-4a5b-81a1-cea1710afb35.2.13.3"),sQuery(id+"F0.wireOp",EDGE,"c2419bcc-613f-4a5b-81a1-cea1710afb35.3.0.0"),sQuery(id+"F0.wireOp",EDGE,"c2419bcc-613f-4a5b-81a1-cea1710afb35.3.0.1"),sQuery(id+"F0.wireOp",EDGE,"c2419bcc-613f-4a5b-81a1-cea1710afb35.3.0.2"),sQuery(id+"F0.wireOp",EDGE,"c2419bcc-613f-4a5b-81a1-cea1710afb35.3.0.3"),sQuery(id+"F0.wireOp",EDGE,"c2419bcc-613f-4a5b-81a1-cea1710afb35.3.1.0"),sQuery(id+"F0.wireOp",EDGE,"c2419bcc-613f-4a5b-81a1-cea1710afb35.3.1.1"),sQuery(id+"F0.wireOp",EDGE,"c2419bcc-613f-4a5b-81a1-cea1710afb35.3.1.2"),sQuery(id+"F0.wireOp",EDGE,"c2419bcc-613f-4a5b-81a1-cea1710afb35.3.1.3"),sQuery(id+"F0.wireOp",EDGE,"c2419bcc-613f-4a5b-81a1-cea1710afb35.3.2.0"),sQuery(id+"F0.wireOp",EDGE,"c2419bcc-613f-4a5b-81a1-cea1710afb35.3.2.1"),sQuery(id+"F0.wireOp",EDGE,"c2419bcc-613f-4a5b-81a1-cea1710afb35.3.2.2"),sQuery(id+"F0.wireOp",EDGE,"c2419bcc-613f-4a5b-81a1-cea1710afb35.3.2.3"),sQuery(id+"F0.wireOp",EDGE,"c2419bcc-613f-4a5b-81a1-cea1710afb35.3.3.0"),sQuery(id+"F0.wireOp",EDGE,"c2419bcc-613f-4a5b-81a1-cea1710afb35.3.3.1"),sQuery(id+"F0.wireOp",EDGE,"c2419bcc-613f-4a5b-81a1-cea1710afb35.3.3.2"),sQuery(id+"F0.wireOp",EDGE,"c2419bcc-613f-4a5b-81a1-cea1710afb35.3.3.3"),sQuery(id+"F0.wireOp",EDGE,"c2419bcc-613f-4a5b-81a1-cea1710afb35.3.4.0"),sQuery(id+"F0.wireOp",EDGE,"c2419bcc-613f-4a5b-81a1-cea1710afb35.3.4.1"),sQuery(id+"F0.wireOp",EDGE,"c2419bcc-613f-4a5b-81a1-cea1710afb35.3.4.2"),sQuery(id+"F0.wireOp",EDGE,"c2419bcc-613f-4a5b-81a1-cea1710afb35.3.4.3"),sQuery(id+"F0.wireOp",EDGE,"c2419bcc-613f-4a5b-81a1-cea1710afb35.3.5.0"),sQuery(id+"F0.wireOp",EDGE,"c2419bcc-613f-4a5b-81a1-cea1710afb35.3.5.1"),sQuery(id+"F0.wireOp",EDGE,"c2419bcc-613f-4a5b-81a1-cea1710afb35.3.5.2"),sQuery(id+"F0.wireOp",EDGE,"c2419bcc-613f-4a5b-81a1-cea1710afb35.3.5.3"),sQuery(id+"F0.wireOp",EDGE,"c2419bcc-613f-4a5b-81a1-cea1710afb35.3.6.0"),sQuery(id+"F0.wireOp",EDGE,"c2419bcc-613f-4a5b-81a1-cea1710afb35.3.6.1"),sQuery(id+"F0.wireOp",EDGE,"c2419bcc-613f-4a5b-81a1-cea1710afb35.3.6.2"),sQuery(id+"F0.wireOp",EDGE,"c2419bcc-613f-4a5b-81a1-cea1710afb35.3.6.3"),sQuery(id+"F0.wireOp",EDGE,"c2419bcc-613f-4a5b-81a1-cea1710afb35.3.7.0"),sQuery(id+"F0.wireOp",EDGE,"c2419bcc-613f-4a5b-81a1-cea1710afb35.3.7.1"),sQuery(id+"F0.wireOp",EDGE,"c2419bcc-613f-4a5b-81a1-cea1710afb35.3.7.2"),sQuery(id+"F0.wireOp",EDGE,"c2419bcc-613f-4a5b-81a1-cea1710afb35.3.7.3"),sQuery(id+"F0.wireOp",EDGE,"c2419bcc-613f-4a5b-81a1-cea1710afb35.3.8.0"),sQuery(id+"F0.wireOp",EDGE,"c2419bcc-613f-4a5b-81a1-cea1710afb35.3.8.1"),sQuery(id+"F0.wireOp",EDGE,"c2419bcc-613f-4a5b-81a1-cea1710afb35.3.8.2"),sQuery(id+"F0.wireOp",EDGE,"c2419bcc-613f-4a5b-81a1-cea1710afb35.3.8.3"),sQuery(id+"F0.wireOp",EDGE,"c2419bcc-613f-4a5b-81a1-cea1710afb35.3.9.0"),sQuery(id+"F0.wireOp",EDGE,"c2419bcc-613f-4a5b-81a1-cea1710afb35.3.9.1"),sQuery(id+"F0.wireOp",EDGE,"c2419bcc-613f-4a5b-81a1-cea1710afb35.3.9.2"),sQuery(id+"F0.wireOp",EDGE,"c2419bcc-613f-4a5b-81a1-cea1710afb35.3.9.3"),sQuery(id+"F0.wireOp",EDGE,"c2419bcc-613f-4a5b-81a1-cea1710afb35.3.10.0"),sQuery(id+"F0.wireOp",EDGE,"c2419bcc-613f-4a5b-81a1-cea1710afb35.3.10.1"),sQuery(id+"F0.wireOp",EDGE,"c2419bcc-613f-4a5b-81a1-cea1710afb35.3.10.2"),sQuery(id+"F0.wireOp",EDGE,"c2419bcc-613f-4a5b-81a1-cea1710afb35.3.10.3"),sQuery(id+"F0.wireOp",EDGE,"c2419bcc-613f-4a5b-81a1-cea1710afb35.3.11.0"),sQuery(id+"F0.wireOp",EDGE,"c2419bcc-613f-4a5b-81a1-cea1710afb35.3.11.1"),sQuery(id+"F0.wireOp",EDGE,"c2419bcc-613f-4a5b-81a1-cea1710afb35.3.11.2"),sQuery(id+"F0.wireOp",EDGE,"c2419bcc-613f-4a5b-81a1-cea1710afb35.3.11.3"),sQuery(id+"F0.wireOp",EDGE,"c2419bcc-613f-4a5b-81a1-cea1710afb35.3.12.0"),sQuery(id+"F0.wireOp",EDGE,"c2419bcc-613f-4a5b-81a1-cea1710afb35.3.12.1"),sQuery(id+"F0.wireOp",EDGE,"c2419bcc-613f-4a5b-81a1-cea1710afb35.3.12.2"),sQuery(id+"F0.wireOp",EDGE,"c2419bcc-613f-4a5b-81a1-cea1710afb35.3.12.3"),sQuery(id+"F0.wireOp",EDGE,"c2419bcc-613f-4a5b-81a1-cea1710afb35.3.13.0"),sQuery(id+"F0.wireOp",EDGE,"c2419bcc-613f-4a5b-81a1-cea1710afb35.3.13.1"),sQuery(id+"F0.wireOp",EDGE,"c2419bcc-613f-4a5b-81a1-cea1710afb35.3.13.2"),sQuery(id+"F0.wireOp",EDGE,"c2419bcc-613f-4a5b-81a1-cea1710afb35.3.13.3"),sQuery(id+"F0.wireOp",EDGE,"c2419bcc-613f-4a5b-81a1-cea1710afb35.4.0.0"),sQuery(id+"F0.wireOp",EDGE,"c2419bcc-613f-4a5b-81a1-cea1710afb35.4.0.1"),sQuery(id+"F0.wireOp",EDGE,"c2419bcc-613f-4a5b-81a1-cea1710afb35.4.0.2"),sQuery(id+"F0.wireOp",EDGE,"c2419bcc-613f-4a5b-81a1-cea1710afb35.4.0.3"),sQuery(id+"F0.wireOp",EDGE,"c2419bcc-613f-4a5b-81a1-cea1710afb35.4.1.0"),sQuery(id+"F0.wireOp",EDGE,"c2419bcc-613f-4a5b-81a1-cea1710afb35.4.1.1"),sQuery(id+"F0.wireOp",EDGE,"c2419bcc-613f-4a5b-81a1-cea1710afb35.4.1.2"),sQuery(id+"F0.wireOp",EDGE,"c2419bcc-613f-4a5b-81a1-cea1710afb35.4.1.3"),sQuery(id+"F0.wireOp",EDGE,"c2419bcc-613f-4a5b-81a1-cea1710afb35.4.2.0"),sQuery(id+"F0.wireOp",EDGE,"c2419bcc-613f-4a5b-81a1-cea1710afb35.4.2.1"),sQuery(id+"F0.wireOp",EDGE,"c2419bcc-613f-4a5b-81a1-cea1710afb35.4.2.2"),sQuery(id+"F0.wireOp",EDGE,"c2419bcc-613f-4a5b-81a1-cea1710afb35.4.2.3"),sQuery(id+"F0.wireOp",EDGE,"c2419bcc-613f-4a5b-81a1-cea1710afb35.4.3.0"),sQuery(id+"F0.wireOp",EDGE,"c2419bcc-613f-4a5b-81a1-cea1710afb35.4.3.1"),sQuery(id+"F0.wireOp",EDGE,"c2419bcc-613f-4a5b-81a1-cea1710afb35.4.3.2"),sQuery(id+"F0.wireOp",EDGE,"c2419bcc-613f-4a5b-81a1-cea1710afb35.4.3.3"),sQuery(id+"F0.wireOp",EDGE,"c2419bcc-613f-4a5b-81a1-cea1710afb35.4.4.0"),sQuery(id+"F0.wireOp",EDGE,"c2419bcc-613f-4a5b-81a1-cea1710afb35.4.4.1"),sQuery(id+"F0.wireOp",EDGE,"c2419bcc-613f-4a5b-81a1-cea1710afb35.4.4.2"),sQuery(id+"F0.wireOp",EDGE,"c2419bcc-613f-4a5b-81a1-cea1710afb35.4.4.3"),sQuery(id+"F0.wireOp",EDGE,"c2419bcc-613f-4a5b-81a1-cea1710afb35.4.5.0"),sQuery(id+"F0.wireOp",EDGE,"c2419bcc-613f-4a5b-81a1-cea1710afb35.4.5.1"),sQuery(id+"F0.wireOp",EDGE,"c2419bcc-613f-4a5b-81a1-cea1710afb35.4.5.2"),sQuery(id+"F0.wireOp",EDGE,"c2419bcc-613f-4a5b-81a1-cea1710afb35.4.5.3"),sQuery(id+"F0.wireOp",EDGE,"c2419bcc-613f-4a5b-81a1-cea1710afb35.4.6.0"),sQuery(id+"F0.wireOp",EDGE,"c2419bcc-613f-4a5b-81a1-cea1710afb35.4.6.1"),sQuery(id+"F0.wireOp",EDGE,"c2419bcc-613f-4a5b-81a1-cea1710afb35.4.6.2"),sQuery(id+"F0.wireOp",EDGE,"c2419bcc-613f-4a5b-81a1-cea1710afb35.4.6.3"),sQuery(id+"F0.wireOp",EDGE,"c2419bcc-613f-4a5b-81a1-cea1710afb35.4.7.0"),sQuery(id+"F0.wireOp",EDGE,"c2419bcc-613f-4a5b-81a1-cea1710afb35.4.7.1"),sQuery(id+"F0.wireOp",EDGE,"c2419bcc-613f-4a5b-81a1-cea1710afb35.4.7.2"),sQuery(id+"F0.wireOp",EDGE,"c2419bcc-613f-4a5b-81a1-cea1710afb35.4.7.3"),sQuery(id+"F0.wireOp",EDGE,"c2419bcc-613f-4a5b-81a1-cea1710afb35.4.8.0"),sQuery(id+"F0.wireOp",EDGE,"c2419bcc-613f-4a5b-81a1-cea1710afb35.4.8.1"),sQuery(id+"F0.wireOp",EDGE,"c2419bcc-613f-4a5b-81a1-cea1710afb35.4.8.2"),sQuery(id+"F0.wireOp",EDGE,"c2419bcc-613f-4a5b-81a1-cea1710afb35.4.8.3"),sQuery(id+"F0.wireOp",EDGE,"c2419bcc-613f-4a5b-81a1-cea1710afb35.4.9.0"),sQuery(id+"F0.wireOp",EDGE,"c2419bcc-613f-4a5b-81a1-cea1710afb35.4.9.1"),sQuery(id+"F0.wireOp",EDGE,"c2419bcc-613f-4a5b-81a1-cea1710afb35.4.9.2"),sQuery(id+"F0.wireOp",EDGE,"c2419bcc-613f-4a5b-81a1-cea1710afb35.4.9.3"),sQuery(id+"F0.wireOp",EDGE,"c2419bcc-613f-4a5b-81a1-cea1710afb35.4.10.0"),sQuery(id+"F0.wireOp",EDGE,"c2419bcc-613f-4a5b-81a1-cea1710afb35.4.10.1"),sQuery(id+"F0.wireOp",EDGE,"c2419bcc-613f-4a5b-81a1-cea1710afb35.4.10.2"),sQuery(id+"F0.wireOp",EDGE,"c2419bcc-613f-4a5b-81a1-cea1710afb35.4.10.3"),sQuery(id+"F0.wireOp",EDGE,"c2419bcc-613f-4a5b-81a1-cea1710afb35.4.11.0"),sQuery(id+"F0.wireOp",EDGE,"c2419bcc-613f-4a5b-81a1-cea1710afb35.4.11.1"),sQuery(id+"F0.wireOp",EDGE,"c2419bcc-613f-4a5b-81a1-cea1710afb35.4.11.2"),sQuery(id+"F0.wireOp",EDGE,"c2419bcc-613f-4a5b-81a1-cea1710afb35.4.11.3"),sQuery(id+"F0.wireOp",EDGE,"c2419bcc-613f-4a5b-81a1-cea1710afb35.4.12.0"),sQuery(id+"F0.wireOp",EDGE,"c2419bcc-613f-4a5b-81a1-cea1710afb35.4.12.1"),sQuery(id+"F0.wireOp",EDGE,"c2419bcc-613f-4a5b-81a1-cea1710afb35.4.12.2"),sQuery(id+"F0.wireOp",EDGE,"c2419bcc-613f-4a5b-81a1-cea1710afb35.4.12.3"),sQuery(id+"F0.wireOp",EDGE,"c2419bcc-613f-4a5b-81a1-cea1710afb35.4.13.0"),sQuery(id+"F0.wireOp",EDGE,"c2419bcc-613f-4a5b-81a1-cea1710afb35.4.13.1"),sQuery(id+"F0.wireOp",EDGE,"c2419bcc-613f-4a5b-81a1-cea1710afb35.4.13.2"),sQuery(id+"F0.wireOp",EDGE,"c2419bcc-613f-4a5b-81a1-cea1710afb35.4.13.3"),sQuery(id+"F0.wireOp",EDGE,"c2419bcc-613f-4a5b-81a1-cea1710afb35.5.0.0"),sQuery(id+"F0.wireOp",EDGE,"c2419bcc-613f-4a5b-81a1-cea1710afb35.5.0.1"),sQuery(id+"F0.wireOp",EDGE,"c2419bcc-613f-4a5b-81a1-cea1710afb35.5.0.2"),sQuery(id+"F0.wireOp",EDGE,"c2419bcc-613f-4a5b-81a1-cea1710afb35.5.0.3"),sQuery(id+"F0.wireOp",EDGE,"c2419bcc-613f-4a5b-81a1-cea1710afb35.5.1.0"),sQuery(id+"F0.wireOp",EDGE,"c2419bcc-613f-4a5b-81a1-cea1710afb35.5.1.1"),sQuery(id+"F0.wireOp",EDGE,"c2419bcc-613f-4a5b-81a1-cea1710afb35.5.1.2"),sQuery(id+"F0.wireOp",EDGE,"c2419bcc-613f-4a5b-81a1-cea1710afb35.5.1.3"),sQuery(id+"F0.wireOp",EDGE,"c2419bcc-613f-4a5b-81a1-cea1710afb35.5.2.0"),sQuery(id+"F0.wireOp",EDGE,"c2419bcc-613f-4a5b-81a1-cea1710afb35.5.2.1"),sQuery(id+"F0.wireOp",EDGE,"c2419bcc-613f-4a5b-81a1-cea1710afb35.5.2.2"),sQuery(id+"F0.wireOp",EDGE,"c2419bcc-613f-4a5b-81a1-cea1710afb35.5.2.3"),sQuery(id+"F0.wireOp",EDGE,"c2419bcc-613f-4a5b-81a1-cea1710afb35.5.3.0"),sQuery(id+"F0.wireOp",EDGE,"c2419bcc-613f-4a5b-81a1-cea1710afb35.5.3.1"),sQuery(id+"F0.wireOp",EDGE,"c2419bcc-613f-4a5b-81a1-cea1710afb35.5.3.2"),sQuery(id+"F0.wireOp",EDGE,"c2419bcc-613f-4a5b-81a1-cea1710afb35.5.3.3"),sQuery(id+"F0.wireOp",EDGE,"c2419bcc-613f-4a5b-81a1-cea1710afb35.5.4.0"),sQuery(id+"F0.wireOp",EDGE,"c2419bcc-613f-4a5b-81a1-cea1710afb35.5.4.1"),sQuery(id+"F0.wireOp",EDGE,"c2419bcc-613f-4a5b-81a1-cea1710afb35.5.4.2"),sQuery(id+"F0.wireOp",EDGE,"c2419bcc-613f-4a5b-81a1-cea1710afb35.5.4.3"),sQuery(id+"F0.wireOp",EDGE,"c2419bcc-613f-4a5b-81a1-cea1710afb35.5.5.0"),sQuery(id+"F0.wireOp",EDGE,"c2419bcc-613f-4a5b-81a1-cea1710afb35.5.5.1"),sQuery(id+"F0.wireOp",EDGE,"c2419bcc-613f-4a5b-81a1-cea1710afb35.5.5.2"),sQuery(id+"F0.wireOp",EDGE,"c2419bcc-613f-4a5b-81a1-cea1710afb35.5.5.3"),sQuery(id+"F0.wireOp",EDGE,"c2419bcc-613f-4a5b-81a1-cea1710afb35.5.6.0"),sQuery(id+"F0.wireOp",EDGE,"c2419bcc-613f-4a5b-81a1-cea1710afb35.5.6.1"),sQuery(id+"F0.wireOp",EDGE,"c2419bcc-613f-4a5b-81a1-cea1710afb35.5.6.2"),sQuery(id+"F0.wireOp",EDGE,"c2419bcc-613f-4a5b-81a1-cea1710afb35.5.6.3"),sQuery(id+"F0.wireOp",EDGE,"c2419bcc-613f-4a5b-81a1-cea1710afb35.5.7.0"),sQuery(id+"F0.wireOp",EDGE,"c2419bcc-613f-4a5b-81a1-cea1710afb35.5.7.1"),sQuery(id+"F0.wireOp",EDGE,"c2419bcc-613f-4a5b-81a1-cea1710afb35.5.7.2"),sQuery(id+"F0.wireOp",EDGE,"c2419bcc-613f-4a5b-81a1-cea1710afb35.5.7.3"),sQuery(id+"F0.wireOp",EDGE,"c2419bcc-613f-4a5b-81a1-cea1710afb35.5.8.0"),sQuery(id+"F0.wireOp",EDGE,"c2419bcc-613f-4a5b-81a1-cea1710afb35.5.8.1"),sQuery(id+"F0.wireOp",EDGE,"c2419bcc-613f-4a5b-81a1-cea1710afb35.5.8.2"),sQuery(id+"F0.wireOp",EDGE,"c2419bcc-613f-4a5b-81a1-cea1710afb35.5.8.3"),sQuery(id+"F0.wireOp",EDGE,"c2419bcc-613f-4a5b-81a1-cea1710afb35.5.9.0"),sQuery(id+"F0.wireOp",EDGE,"c2419bcc-613f-4a5b-81a1-cea1710afb35.5.9.1"),sQuery(id+"F0.wireOp",EDGE,"c2419bcc-613f-4a5b-81a1-cea1710afb35.5.9.2"),sQuery(id+"F0.wireOp",EDGE,"c2419bcc-613f-4a5b-81a1-cea1710afb35.5.9.3"),sQuery(id+"F0.wireOp",EDGE,"c2419bcc-613f-4a5b-81a1-cea1710afb35.5.10.0"),sQuery(id+"F0.wireOp",EDGE,"c2419bcc-613f-4a5b-81a1-cea1710afb35.5.10.1"),sQuery(id+"F0.wireOp",EDGE,"c2419bcc-613f-4a5b-81a1-cea1710afb35.5.10.2"),sQuery(id+"F0.wireOp",EDGE,"c2419bcc-613f-4a5b-81a1-cea1710afb35.5.10.3"),sQuery(id+"F0.wireOp",EDGE,"c2419bcc-613f-4a5b-81a1-cea1710afb35.5.11.0"),sQuery(id+"F0.wireOp",EDGE,"c2419bcc-613f-4a5b-81a1-cea1710afb35.5.11.1"),sQuery(id+"F0.wireOp",EDGE,"c2419bcc-613f-4a5b-81a1-cea1710afb35.5.11.2"),sQuery(id+"F0.wireOp",EDGE,"c2419bcc-613f-4a5b-81a1-cea1710afb35.5.11.3"),sQuery(id+"F0.wireOp",EDGE,"c2419bcc-613f-4a5b-81a1-cea1710afb35.5.12.0"),sQuery(id+"F0.wireOp",EDGE,"c2419bcc-613f-4a5b-81a1-cea1710afb35.5.12.1"),sQuery(id+"F0.wireOp",EDGE,"c2419bcc-613f-4a5b-81a1-cea1710afb35.5.12.2"),sQuery(id+"F0.wireOp",EDGE,"c2419bcc-613f-4a5b-81a1-cea1710afb35.5.12.3"),sQuery(id+"F0.wireOp",EDGE,"c2419bcc-613f-4a5b-81a1-cea1710afb35.5.13.0"),sQuery(id+"F0.wireOp",EDGE,"c2419bcc-613f-4a5b-81a1-cea1710afb35.5.13.1"),sQuery(id+"F0.wireOp",EDGE,"c2419bcc-613f-4a5b-81a1-cea1710afb35.5.13.2"),sQuery(id+"F0.wireOp",EDGE,"c2419bcc-613f-4a5b-81a1-cea1710afb35.5.13.3"),sQuery(id+"F0.wireOp",EDGE,"c2419bcc-613f-4a5b-81a1-cea1710afb35.6.0.0"),sQuery(id+"F0.wireOp",EDGE,"c2419bcc-613f-4a5b-81a1-cea1710afb35.6.0.1"),sQuery(id+"F0.wireOp",EDGE,"c2419bcc-613f-4a5b-81a1-cea1710afb35.6.0.2"),sQuery(id+"F0.wireOp",EDGE,"c2419bcc-613f-4a5b-81a1-cea1710afb35.6.0.3"),sQuery(id+"F0.wireOp",EDGE,"c2419bcc-613f-4a5b-81a1-cea1710afb35.6.1.0"),sQuery(id+"F0.wireOp",EDGE,"c2419bcc-613f-4a5b-81a1-cea1710afb35.6.1.1"),sQuery(id+"F0.wireOp",EDGE,"c2419bcc-613f-4a5b-81a1-cea1710afb35.6.1.2"),sQuery(id+"F0.wireOp",EDGE,"c2419bcc-613f-4a5b-81a1-cea1710afb35.6.1.3"),sQuery(id+"F0.wireOp",EDGE,"c2419bcc-613f-4a5b-81a1-cea1710afb35.6.2.0"),sQuery(id+"F0.wireOp",EDGE,"c2419bcc-613f-4a5b-81a1-cea1710afb35.6.2.1"),sQuery(id+"F0.wireOp",EDGE,"c2419bcc-613f-4a5b-81a1-cea1710afb35.6.2.2"),sQuery(id+"F0.wireOp",EDGE,"c2419bcc-613f-4a5b-81a1-cea1710afb35.6.2.3"),sQuery(id+"F0.wireOp",EDGE,"c2419bcc-613f-4a5b-81a1-cea1710afb35.6.3.0"),sQuery(id+"F0.wireOp",EDGE,"c2419bcc-613f-4a5b-81a1-cea1710afb35.6.3.1"),sQuery(id+"F0.wireOp",EDGE,"c2419bcc-613f-4a5b-81a1-cea1710afb35.6.3.2"),sQuery(id+"F0.wireOp",EDGE,"c2419bcc-613f-4a5b-81a1-cea1710afb35.6.3.3"),sQuery(id+"F0.wireOp",EDGE,"c2419bcc-613f-4a5b-81a1-cea1710afb35.6.4.0"),sQuery(id+"F0.wireOp",EDGE,"c2419bcc-613f-4a5b-81a1-cea1710afb35.6.4.1"),sQuery(id+"F0.wireOp",EDGE,"c2419bcc-613f-4a5b-81a1-cea1710afb35.6.4.2"),sQuery(id+"F0.wireOp",EDGE,"c2419bcc-613f-4a5b-81a1-cea1710afb35.6.4.3"),sQuery(id+"F0.wireOp",EDGE,"c2419bcc-613f-4a5b-81a1-cea1710afb35.6.5.0"),sQuery(id+"F0.wireOp",EDGE,"c2419bcc-613f-4a5b-81a1-cea1710afb35.6.5.1"),sQuery(id+"F0.wireOp",EDGE,"c2419bcc-613f-4a5b-81a1-cea1710afb35.6.5.2"),sQuery(id+"F0.wireOp",EDGE,"c2419bcc-613f-4a5b-81a1-cea1710afb35.6.5.3"),sQuery(id+"F0.wireOp",EDGE,"c2419bcc-613f-4a5b-81a1-cea1710afb35.6.6.0"),sQuery(id+"F0.wireOp",EDGE,"c2419bcc-613f-4a5b-81a1-cea1710afb35.6.6.1"),sQuery(id+"F0.wireOp",EDGE,"c2419bcc-613f-4a5b-81a1-cea1710afb35.6.6.2"),sQuery(id+"F0.wireOp",EDGE,"c2419bcc-613f-4a5b-81a1-cea1710afb35.6.6.3"),sQuery(id+"F0.wireOp",EDGE,"c2419bcc-613f-4a5b-81a1-cea1710afb35.6.7.0"),sQuery(id+"F0.wireOp",EDGE,"c2419bcc-613f-4a5b-81a1-cea1710afb35.6.7.1"),sQuery(id+"F0.wireOp",EDGE,"c2419bcc-613f-4a5b-81a1-cea1710afb35.6.7.2"),sQuery(id+"F0.wireOp",EDGE,"c2419bcc-613f-4a5b-81a1-cea1710afb35.6.7.3"),sQuery(id+"F0.wireOp",EDGE,"c2419bcc-613f-4a5b-81a1-cea1710afb35.6.8.0"),sQuery(id+"F0.wireOp",EDGE,"c2419bcc-613f-4a5b-81a1-cea1710afb35.6.8.1"),sQuery(id+"F0.wireOp",EDGE,"c2419bcc-613f-4a5b-81a1-cea1710afb35.6.8.2"),sQuery(id+"F0.wireOp",EDGE,"c2419bcc-613f-4a5b-81a1-cea1710afb35.6.8.3"),sQuery(id+"F0.wireOp",EDGE,"c2419bcc-613f-4a5b-81a1-cea1710afb35.6.9.0"),sQuery(id+"F0.wireOp",EDGE,"c2419bcc-613f-4a5b-81a1-cea1710afb35.6.9.1"),sQuery(id+"F0.wireOp",EDGE,"c2419bcc-613f-4a5b-81a1-cea1710afb35.6.9.2"),sQuery(id+"F0.wireOp",EDGE,"c2419bcc-613f-4a5b-81a1-cea1710afb35.6.9.3"),sQuery(id+"F0.wireOp",EDGE,"c2419bcc-613f-4a5b-81a1-cea1710afb35.6.10.0"),sQuery(id+"F0.wireOp",EDGE,"c2419bcc-613f-4a5b-81a1-cea1710afb35.6.10.1"),sQuery(id+"F0.wireOp",EDGE,"c2419bcc-613f-4a5b-81a1-cea1710afb35.6.10.2"),sQuery(id+"F0.wireOp",EDGE,"c2419bcc-613f-4a5b-81a1-cea1710afb35.6.10.3"),sQuery(id+"F0.wireOp",EDGE,"c2419bcc-613f-4a5b-81a1-cea1710afb35.6.11.0"),sQuery(id+"F0.wireOp",EDGE,"c2419bcc-613f-4a5b-81a1-cea1710afb35.6.11.1"),sQuery(id+"F0.wireOp",EDGE,"c2419bcc-613f-4a5b-81a1-cea1710afb35.6.11.2"),sQuery(id+"F0.wireOp",EDGE,"c2419bcc-613f-4a5b-81a1-cea1710afb35.6.11.3"),sQuery(id+"F0.wireOp",EDGE,"c2419bcc-613f-4a5b-81a1-cea1710afb35.6.12.0"),sQuery(id+"F0.wireOp",EDGE,"c2419bcc-613f-4a5b-81a1-cea1710afb35.6.12.1"),sQuery(id+"F0.wireOp",EDGE,"c2419bcc-613f-4a5b-81a1-cea1710afb35.6.12.2"),sQuery(id+"F0.wireOp",EDGE,"c2419bcc-613f-4a5b-81a1-cea1710afb35.6.12.3"),sQuery(id+"F0.wireOp",EDGE,"c2419bcc-613f-4a5b-81a1-cea1710afb35.6.13.0"),sQuery(id+"F0.wireOp",EDGE,"c2419bcc-613f-4a5b-81a1-cea1710afb35.6.13.1"),sQuery(id+"F0.wireOp",EDGE,"c2419bcc-613f-4a5b-81a1-cea1710afb35.6.13.2"),sQuery(id+"F0.wireOp",EDGE,"c2419bcc-613f-4a5b-81a1-cea1710afb35.6.13.3"),sQuery(id+"F0.wireOp",EDGE,"c2419bcc-613f-4a5b-81a1-cea1710afb35.7.0.0"),sQuery(id+"F0.wireOp",EDGE,"c2419bcc-613f-4a5b-81a1-cea1710afb35.7.0.1"),sQuery(id+"F0.wireOp",EDGE,"c2419bcc-613f-4a5b-81a1-cea1710afb35.7.0.2"),sQuery(id+"F0.wireOp",EDGE,"c2419bcc-613f-4a5b-81a1-cea1710afb35.7.0.3"),sQuery(id+"F0.wireOp",EDGE,"c2419bcc-613f-4a5b-81a1-cea1710afb35.7.1.0"),sQuery(id+"F0.wireOp",EDGE,"c2419bcc-613f-4a5b-81a1-cea1710afb35.7.1.1"),sQuery(id+"F0.wireOp",EDGE,"c2419bcc-613f-4a5b-81a1-cea1710afb35.7.1.2"),sQuery(id+"F0.wireOp",EDGE,"c2419bcc-613f-4a5b-81a1-cea1710afb35.7.1.3"),sQuery(id+"F0.wireOp",EDGE,"c2419bcc-613f-4a5b-81a1-cea1710afb35.7.2.0"),sQuery(id+"F0.wireOp",EDGE,"c2419bcc-613f-4a5b-81a1-cea1710afb35.7.2.1"),sQuery(id+"F0.wireOp",EDGE,"c2419bcc-613f-4a5b-81a1-cea1710afb35.7.2.2"),sQuery(id+"F0.wireOp",EDGE,"c2419bcc-613f-4a5b-81a1-cea1710afb35.7.2.3"),sQuery(id+"F0.wireOp",EDGE,"c2419bcc-613f-4a5b-81a1-cea1710afb35.7.3.0"),sQuery(id+"F0.wireOp",EDGE,"c2419bcc-613f-4a5b-81a1-cea1710afb35.7.3.1"),sQuery(id+"F0.wireOp",EDGE,"c2419bcc-613f-4a5b-81a1-cea1710afb35.7.3.2"),sQuery(id+"F0.wireOp",EDGE,"c2419bcc-613f-4a5b-81a1-cea1710afb35.7.3.3"),sQuery(id+"F0.wireOp",EDGE,"c2419bcc-613f-4a5b-81a1-cea1710afb35.7.4.0"),sQuery(id+"F0.wireOp",EDGE,"c2419bcc-613f-4a5b-81a1-cea1710afb35.7.4.1"),sQuery(id+"F0.wireOp",EDGE,"c2419bcc-613f-4a5b-81a1-cea1710afb35.7.4.2"),sQuery(id+"F0.wireOp",EDGE,"c2419bcc-613f-4a5b-81a1-cea1710afb35.7.4.3"),sQuery(id+"F0.wireOp",EDGE,"c2419bcc-613f-4a5b-81a1-cea1710afb35.7.5.0"),sQuery(id+"F0.wireOp",EDGE,"c2419bcc-613f-4a5b-81a1-cea1710afb35.7.5.1"),sQuery(id+"F0.wireOp",EDGE,"c2419bcc-613f-4a5b-81a1-cea1710afb35.7.5.2"),sQuery(id+"F0.wireOp",EDGE,"c2419bcc-613f-4a5b-81a1-cea1710afb35.7.5.3"),sQuery(id+"F0.wireOp",EDGE,"c2419bcc-613f-4a5b-81a1-cea1710afb35.7.6.0"),sQuery(id+"F0.wireOp",EDGE,"c2419bcc-613f-4a5b-81a1-cea1710afb35.7.6.1"),sQuery(id+"F0.wireOp",EDGE,"c2419bcc-613f-4a5b-81a1-cea1710afb35.7.6.2"),sQuery(id+"F0.wireOp",EDGE,"c2419bcc-613f-4a5b-81a1-cea1710afb35.7.6.3"),sQuery(id+"F0.wireOp",EDGE,"c2419bcc-613f-4a5b-81a1-cea1710afb35.7.7.0"),sQuery(id+"F0.wireOp",EDGE,"c2419bcc-613f-4a5b-81a1-cea1710afb35.7.7.1"),sQuery(id+"F0.wireOp",EDGE,"c2419bcc-613f-4a5b-81a1-cea1710afb35.7.7.2"),sQuery(id+"F0.wireOp",EDGE,"c2419bcc-613f-4a5b-81a1-cea1710afb35.7.7.3"),sQuery(id+"F0.wireOp",EDGE,"c2419bcc-613f-4a5b-81a1-cea1710afb35.7.8.0"),sQuery(id+"F0.wireOp",EDGE,"c2419bcc-613f-4a5b-81a1-cea1710afb35.7.8.1"),sQuery(id+"F0.wireOp",EDGE,"c2419bcc-613f-4a5b-81a1-cea1710afb35.7.8.2"),sQuery(id+"F0.wireOp",EDGE,"c2419bcc-613f-4a5b-81a1-cea1710afb35.7.8.3"),sQuery(id+"F0.wireOp",EDGE,"c2419bcc-613f-4a5b-81a1-cea1710afb35.7.9.0"),sQuery(id+"F0.wireOp",EDGE,"c2419bcc-613f-4a5b-81a1-cea1710afb35.7.9.1"),sQuery(id+"F0.wireOp",EDGE,"c2419bcc-613f-4a5b-81a1-cea1710afb35.7.9.2"),sQuery(id+"F0.wireOp",EDGE,"c2419bcc-613f-4a5b-81a1-cea1710afb35.7.9.3"),sQuery(id+"F0.wireOp",EDGE,"c2419bcc-613f-4a5b-81a1-cea1710afb35.7.10.0"),sQuery(id+"F0.wireOp",EDGE,"c2419bcc-613f-4a5b-81a1-cea1710afb35.7.10.1"),sQuery(id+"F0.wireOp",EDGE,"c2419bcc-613f-4a5b-81a1-cea1710afb35.7.10.2"),sQuery(id+"F0.wireOp",EDGE,"c2419bcc-613f-4a5b-81a1-cea1710afb35.7.10.3"),sQuery(id+"F0.wireOp",EDGE,"c2419bcc-613f-4a5b-81a1-cea1710afb35.7.11.0"),sQuery(id+"F0.wireOp",EDGE,"c2419bcc-613f-4a5b-81a1-cea1710afb35.7.11.1"),sQuery(id+"F0.wireOp",EDGE,"c2419bcc-613f-4a5b-81a1-cea1710afb35.7.11.2"),sQuery(id+"F0.wireOp",EDGE,"c2419bcc-613f-4a5b-81a1-cea1710afb35.7.11.3"),sQuery(id+"F0.wireOp",EDGE,"c2419bcc-613f-4a5b-81a1-cea1710afb35.7.12.0"),sQuery(id+"F0.wireOp",EDGE,"c2419bcc-613f-4a5b-81a1-cea1710afb35.7.12.1"),sQuery(id+"F0.wireOp",EDGE,"c2419bcc-613f-4a5b-81a1-cea1710afb35.7.12.2"),sQuery(id+"F0.wireOp",EDGE,"c2419bcc-613f-4a5b-81a1-cea1710afb35.7.12.3"),sQuery(id+"F0.wireOp",EDGE,"c2419bcc-613f-4a5b-81a1-cea1710afb35.7.13.0"),sQuery(id+"F0.wireOp",EDGE,"c2419bcc-613f-4a5b-81a1-cea1710afb35.7.13.1"),sQuery(id+"F0.wireOp",EDGE,"c2419bcc-613f-4a5b-81a1-cea1710afb35.7.13.2"),sQuery(id+"F0.wireOp",EDGE,"c2419bcc-613f-4a5b-81a1-cea1710afb35.7.13.3")])],"isStart":true});
            var sketch = newSketch(context, id + "F2", { "sketchPlane" : qUnion([Q0])});
            skLineSegment(sketch, "E345.bottom", {"start": v(-53.01, 123.63) * mm, "end": v(54.49, 123.63) * mm});
            skLineSegment(sketch, "E345.top", {"start": v(-53.01, -66.37) * mm, "end": v(54.49, -66.37) * mm});
            skLineSegment(sketch, "E345.left", {"start": v(-53.01, 123.63) * mm, "end": v(-53.01, -66.37) * mm});
            skLineSegment(sketch, "E345.right", {"start": v(54.49, 123.63) * mm, "end": v(54.49, -66.37) * mm});
            skLineSegment(sketch, "E346.bottom", {"start": v(-50.51, 121.13) * mm, "end": v(51.99, 121.13) * mm});
            skLineSegment(sketch, "E346.top", {"start": v(-50.51, -63.87) * mm, "end": v(51.99, -63.87) * mm});
            skLineSegment(sketch, "E346.left", {"start": v(-50.51, 121.13) * mm, "end": v(-50.51, -63.87) * mm});
            skLineSegment(sketch, "E346.right", {"start": v(51.99, 121.13) * mm, "end": v(51.99, -63.87) * mm});
            skSolve(sketch);
        }
        {
            var Q0;
            Q0 = qSketchRegion(id + "F2", true);
            extrude(context, id + "F3", {"entities" : qUnion([Q0]), "operationType" : NewBodyOperationType.ADD, "depth" : 32.5 * mm});
        }
        {
            var Q0;
            Q0=makeQuery(id+"F3.boolean.opBoolean","MERGE",FACE,{"derivedFrom":[makeQuery(id+"F1.opExtrude","SWEPT_FACE",FACE,{"disambiguationData":[OSD([sQuery(id+"F0.wireOp",EDGE,"E0.left")])]}),makeQuery(id+"F3.opExtrude","SWEPT_FACE",FACE,{"disambiguationData":[OSD([sQuery(id+"F2.wireOp",EDGE,"E345.right")])]})]});
            var sketch = newSketch(context, id + "F4", { "sketchPlane" : qUnion([Q0])});
            skPoint(sketch, "E347.endSnap0", {"position": v(-32.5, 28.63) * mm});
            skLineSegment(sketch, "E348", {"start": v(-4.5, 28.63) * mm, "end": v(-4.5, 84.13) * mm});
            skLineSegment(sketch, "E349", {"start": v(-4.5, 84.13) * mm, "end": v(-32.5, 84.13) * mm});
            skLineSegment(sketch, "E350", {"start": v(-32.5, 84.13) * mm, "end": v(-32.5, 28.63) * mm});
            skLineSegment(sketch, "E351", {"start": v(-4.5, 28.63) * mm, "end": v(-13.64, 28.63) * mm});
            skLineSegment(sketch, "E352.MirrorCS", {"start": v(-4.5, -26.87) * mm, "end": v(-32.5, -26.87) * mm});
            skLineSegment(sketch, "E353.MirrorCS", {"start": v(-32.5, -26.87) * mm, "end": v(-32.5, 28.63) * mm});
            skLineSegment(sketch, "E354.MirrorCS", {"start": v(-4.5, 28.63) * mm, "end": v(-4.5, -26.87) * mm});
            skSolve(sketch);
        }
        {
            var Q0;
            {var subQ0=sQuery(id+"F2.wireOp",EDGE,"E345.bottom");var subQ1=sQuery(id+"F2.wireOp",EDGE,"E346.bottom");var subQ2=sQuery(id+"F2.wireOp",EDGE,"E345.left");var subQ3=sQuery(id+"F2.wireOp",EDGE,"E345.right");var subQ4=sQuery(id+"F2.wireOp",EDGE,"E346.left");var subQ5=sQuery(id+"F2.wireOp",EDGE,"E346.right");Q0=makeQuery(id+"FBptylufdPnb45I_1.boolean.opBoolean","SPLIT",FACE,{"disambiguationData":[TD([makeQuery(id+"F1.opExtrude","SWEPT_FACE",FACE,{"disambiguationData":[OSD([sQuery(id+"F0.wireOp",EDGE,"E0.bottom")])]})])],"derivedFrom":makeQuery(id+"F3.opExtrude","CAP_FACE",FACE,{"disambiguationData":[OSD([subQ0,sQuery(id+"F2.wireOp",EDGE,"E345.top"),subQ2,subQ3,subQ1,sQuery(id+"F2.wireOp",EDGE,"E346.top"),subQ4,subQ5])],"isStart":false})});}
            var sketch = newSketch(context, id + "F5", { "sketchPlane" : qUnion([Q0])});
            skLineSegment(sketch, "E355", {"start": v(-53.01, 123.63) * mm, "end": v(-53.01, -66.37) * mm});
            skLineSegment(sketch, "E356", {"start": v(-53.01, 28.63) * mm, "end": v(68, 28.63) * mm});
            skLineSegment(sketch, "E357", {"start": v(-43.01, 121.13) * mm, "end": v(-43.01, 117.63) * mm});
            skLineSegment(sketch, "E358", {"start": v(-43.01, 117.63) * mm, "end": v(-40.01, 117.63) * mm});
            skLineSegment(sketch, "E359", {"start": v(-40.01, 117.63) * mm, "end": v(-40.01, 121.13) * mm});
            skLineSegment(sketch, "E360", {"start": v(-43.01, 121.13) * mm, "end": v(-40.01, 121.13) * mm});
            skLineSegment(sketch, "E361", {"start": v(0.74, 123.63) * mm, "end": v(0.74, 132.42) * mm});
            skPoint(sketch, "E361.endSnap0", {"position": v(0.74, 123.63) * mm});
            skLineSegment(sketch, "E362.MirrorCS", {"start": v(41.49, 117.63) * mm, "end": v(41.49, 121.13) * mm});
            skLineSegment(sketch, "E363.MirrorCS", {"start": v(44.49, 121.13) * mm, "end": v(41.49, 121.13) * mm});
            skLineSegment(sketch, "E364.MirrorCS", {"start": v(44.49, 117.63) * mm, "end": v(41.49, 117.63) * mm});
            skLineSegment(sketch, "E365.MirrorCS", {"start": v(44.49, 121.13) * mm, "end": v(44.49, 117.63) * mm});
            skLineSegment(sketch, "E366.MirrorCS", {"start": v(-43.01, -63.87) * mm, "end": v(-40.01, -63.87) * mm});
            skLineSegment(sketch, "E367.MirrorCS", {"start": v(-43.01, -63.87) * mm, "end": v(-43.01, -60.37) * mm});
            skLineSegment(sketch, "E368.MirrorCS", {"start": v(41.49, -60.37) * mm, "end": v(41.49, -63.87) * mm});
            skLineSegment(sketch, "E369.MirrorCS", {"start": v(0.74, -66.37) * mm, "end": v(0.74, -75.17) * mm});
            skLineSegment(sketch, "E370.MirrorCS", {"start": v(-40.01, -60.37) * mm, "end": v(-40.01, -63.87) * mm});
            skLineSegment(sketch, "E371.MirrorCS", {"start": v(44.49, -63.87) * mm, "end": v(41.49, -63.87) * mm});
            skLineSegment(sketch, "E372.MirrorCS", {"start": v(-43.01, -60.37) * mm, "end": v(-40.01, -60.37) * mm});
            skLineSegment(sketch, "E373.MirrorCS", {"start": v(44.49, -60.37) * mm, "end": v(41.49, -60.37) * mm});
            skLineSegment(sketch, "E374.MirrorCS", {"start": v(44.49, -63.87) * mm, "end": v(44.49, -60.37) * mm});
            skPoint(sketch, "E375.MirrorP", {"position": v(0.74, -66.37) * mm});
            skSolve(sketch);
        }
        {
            var Q0;
            Q0 = qSketchRegion(id + "F5", true);
            extrude(context, id + "F6", {"entities" : qUnion([Q0]), "operationType" : NewBodyOperationType.ADD, "oppositeDirection" : true, "depth" : 31 * mm});
        }
        {
            var Q0;
            Q0=makeQuery(id+"F6.opExtrude","CAP_EDGE",EDGE,{"disambiguationData":[OSD([sQuery(id+"F5.wireOp",EDGE,"E373.MirrorCS")])],"isStart":false});
            var Q1;
            Q1=makeQuery(id+"F6.opExtrude","CAP_EDGE",EDGE,{"disambiguationData":[OSD([sQuery(id+"F5.wireOp",EDGE,"E372.MirrorCS")])],"isStart":false});
            var Q2;
            Q2=makeQuery(id+"F6.opExtrude","CAP_EDGE",EDGE,{"disambiguationData":[OSD([sQuery(id+"F5.wireOp",EDGE,"E358")])],"isStart":false});
            var Q3;
            Q3=makeQuery(id+"F6.opExtrude","CAP_EDGE",EDGE,{"disambiguationData":[OSD([sQuery(id+"F5.wireOp",EDGE,"E364.MirrorCS")])],"isStart":false});
            chamfer(context, id + "F7", {"entities" : qUnion([Q0, Q1, Q2, Q3]), "chamferType" : ChamferType.TWO_OFFSETS, "width1" : 3.5 * mm, "oppositeDirection" : false, "width2" : 3.5 * mm, "tangentPropagation" : true});
        }
        {
            var Q0;
            {var subQ0=sQuery(id+"F2.wireOp",EDGE,"E345.top");var subQ1=sQuery(id+"F2.wireOp",EDGE,"E346.right");var subQ2=sQuery(id+"F2.wireOp",EDGE,"E345.left");var subQ3=sQuery(id+"F2.wireOp",EDGE,"E345.right");var subQ4=sQuery(id+"F2.wireOp",EDGE,"E346.top");var subQ5=sQuery(id+"F2.wireOp",EDGE,"E346.left");Q0=makeQuery(id+"F6.boolean.opBoolean","MERGE",FACE,{"derivedFrom":[makeQuery(id+"FBptylufdPnb45I_1.boolean.opBoolean","SPLIT",FACE,{"disambiguationData":[TD([makeQuery(id+"F1.opExtrude","SWEPT_FACE",FACE,{"disambiguationData":[OSD([sQuery(id+"F0.wireOp",EDGE,"E0.top")])]})])],"derivedFrom":makeQuery(id+"F3.opExtrude","CAP_FACE",FACE,{"disambiguationData":[OSD([sQuery(id+"F2.wireOp",EDGE,"E345.bottom"),subQ0,subQ2,subQ3,sQuery(id+"F2.wireOp",EDGE,"E346.bottom"),subQ4,subQ5,subQ1])],"isStart":false})}),makeQuery(id+"F6.opExtrude","CAP_FACE",FACE,{"disambiguationData":[OSD([sQuery(id+"F5.wireOp",EDGE,"E366.MirrorCS"),sQuery(id+"F5.wireOp",EDGE,"E367.MirrorCS"),sQuery(id+"F5.wireOp",EDGE,"E370.MirrorCS"),sQuery(id+"F5.wireOp",EDGE,"E372.MirrorCS")])],"isStart":true}),makeQuery(id+"F6.opExtrude","CAP_FACE",FACE,{"disambiguationData":[OSD([sQuery(id+"F5.wireOp",EDGE,"E368.MirrorCS"),sQuery(id+"F5.wireOp",EDGE,"E371.MirrorCS"),sQuery(id+"F5.wireOp",EDGE,"E373.MirrorCS"),sQuery(id+"F5.wireOp",EDGE,"E374.MirrorCS")])],"isStart":true})]});}
            var sketch = newSketch(context, id + "F8", { "sketchPlane" : qUnion([Q0])});
            skLineSegment(sketch, "E376", {"start": v(-53.01, -66.37) * mm, "end": v(-53.01, 123.63) * mm});
            skLineSegment(sketch, "E377", {"start": v(-53.01, 28.63) * mm, "end": v(90.05, 28.63) * mm});
            skLineSegment(sketch, "E378", {"start": v(0.74, -66.37) * mm, "end": v(0.74, -78.4) * mm});
            skLineSegment(sketch, "E379", {"start": v(-43.01, -63.87) * mm, "end": v(-40.01, -63.87) * mm});
            skLineSegment(sketch, "E380", {"start": v(-40.01, -63.87) * mm, "end": v(-40.01, -63.37) * mm});
            skLineSegment(sketch, "E381", {"start": v(-40.01, -63.37) * mm, "end": v(-43.01, -63.37) * mm});
            skLineSegment(sketch, "E382", {"start": v(-43.01, -63.37) * mm, "end": v(-43.01, -63.87) * mm});
            skLineSegment(sketch, "E383.MirrorCS", {"start": v(41.49, -63.87) * mm, "end": v(41.49, -63.37) * mm});
            skLineSegment(sketch, "E384.MirrorCS", {"start": v(44.49, -63.37) * mm, "end": v(44.49, -63.87) * mm});
            skLineSegment(sketch, "E385.MirrorCS", {"start": v(44.49, -63.87) * mm, "end": v(41.49, -63.87) * mm});
            skLineSegment(sketch, "E386.MirrorCS", {"start": v(41.49, -63.37) * mm, "end": v(44.49, -63.37) * mm});
            skLineSegment(sketch, "E387.MirrorCS", {"start": v(-43.01, 121.13) * mm, "end": v(-40.01, 121.13) * mm});
            skLineSegment(sketch, "E388.MirrorCS", {"start": v(-40.01, 121.13) * mm, "end": v(-40.01, 120.63) * mm});
            skLineSegment(sketch, "E389.MirrorCS", {"start": v(-40.01, 120.63) * mm, "end": v(-43.01, 120.63) * mm});
            skLineSegment(sketch, "E390.MirrorCS", {"start": v(-43.01, 120.63) * mm, "end": v(-43.01, 121.13) * mm});
            skLineSegment(sketch, "E391.MirrorCS", {"start": v(41.49, 120.63) * mm, "end": v(44.49, 120.63) * mm});
            skLineSegment(sketch, "E392.MirrorCS", {"start": v(44.49, 121.13) * mm, "end": v(41.49, 121.13) * mm});
            skLineSegment(sketch, "E393.MirrorCS", {"start": v(44.49, 120.63) * mm, "end": v(44.49, 121.13) * mm});
            skLineSegment(sketch, "E394.MirrorCS", {"start": v(41.49, 121.13) * mm, "end": v(41.49, 120.63) * mm});
            skLineSegment(sketch, "E395.MirrorCS", {"start": v(0.74, 123.63) * mm, "end": v(0.74, 135.66) * mm});
            skSolve(sketch);
        }
        {
            var Q0;
            Q0 = qSketchRegion(id + "F8", true);
            extrude(context, id + "F9", {"entities" : qUnion([Q0]), "operationType" : NewBodyOperationType.REMOVE, "oppositeDirection" : true, "depth" : 25 * mm});
        }
        {
            var Q0;
            {var subQ0=sQuery(id+"F5.wireOp",EDGE,"E357");var subQ1=sQuery(id+"F5.wireOp",EDGE,"E358");var subQ2=sQuery(id+"F5.wireOp",EDGE,"E359");var subQ3=sQuery(id+"F2.wireOp",EDGE,"E345.bottom");var subQ4=sQuery(id+"F2.wireOp",EDGE,"E346.bottom");var subQ5=sQuery(id+"F2.wireOp",EDGE,"E345.left");var subQ6=sQuery(id+"F2.wireOp",EDGE,"E345.right");var subQ7=sQuery(id+"F2.wireOp",EDGE,"E346.left");var subQ8=sQuery(id+"F2.wireOp",EDGE,"E346.right");Q0=makeQuery(id+"F9.boolean.opBoolean","SPLIT",FACE,{"disambiguationData":[TD([makeQuery(id+"F6.opExtrude","SWEPT_FACE",FACE,{"disambiguationData":[OSD([subQ0])]})])],"derivedFrom":makeQuery(id+"F6.boolean.opBoolean","MERGE",FACE,{"derivedFrom":[makeQuery(id+"FBptylufdPnb45I_1.boolean.opBoolean","SPLIT",FACE,{"disambiguationData":[TD([makeQuery(id+"F1.opExtrude","SWEPT_FACE",FACE,{"disambiguationData":[OSD([sQuery(id+"F0.wireOp",EDGE,"E0.bottom")])]})])],"derivedFrom":makeQuery(id+"F3.opExtrude","CAP_FACE",FACE,{"disambiguationData":[OSD([subQ3,sQuery(id+"F2.wireOp",EDGE,"E345.top"),subQ5,subQ6,subQ4,sQuery(id+"F2.wireOp",EDGE,"E346.top"),subQ7,subQ8])],"isStart":false})}),makeQuery(id+"F6.opExtrude","CAP_FACE",FACE,{"disambiguationData":[OSD([subQ0,subQ1,subQ2,sQuery(id+"F5.wireOp",EDGE,"E360")])],"isStart":true}),makeQuery(id+"F6.opExtrude","CAP_FACE",FACE,{"disambiguationData":[OSD([sQuery(id+"F5.wireOp",EDGE,"E362.MirrorCS"),sQuery(id+"F5.wireOp",EDGE,"E363.MirrorCS"),sQuery(id+"F5.wireOp",EDGE,"E364.MirrorCS"),sQuery(id+"F5.wireOp",EDGE,"E365.MirrorCS")])],"isStart":true})]})});}
            var Q1;
            {var subQ0=sQuery(id+"F5.wireOp",EDGE,"E362.MirrorCS");var subQ1=sQuery(id+"F5.wireOp",EDGE,"E364.MirrorCS");var subQ2=sQuery(id+"F5.wireOp",EDGE,"E365.MirrorCS");var subQ3=sQuery(id+"F2.wireOp",EDGE,"E345.bottom");var subQ4=sQuery(id+"F2.wireOp",EDGE,"E346.bottom");var subQ5=sQuery(id+"F2.wireOp",EDGE,"E345.left");var subQ6=sQuery(id+"F2.wireOp",EDGE,"E345.right");var subQ7=sQuery(id+"F2.wireOp",EDGE,"E346.left");var subQ8=sQuery(id+"F2.wireOp",EDGE,"E346.right");Q1=makeQuery(id+"F9.boolean.opBoolean","SPLIT",FACE,{"disambiguationData":[TD([makeQuery(id+"F6.opExtrude","SWEPT_FACE",FACE,{"disambiguationData":[OSD([subQ0])]})])],"derivedFrom":makeQuery(id+"F6.boolean.opBoolean","MERGE",FACE,{"derivedFrom":[makeQuery(id+"FBptylufdPnb45I_1.boolean.opBoolean","SPLIT",FACE,{"disambiguationData":[TD([makeQuery(id+"F1.opExtrude","SWEPT_FACE",FACE,{"disambiguationData":[OSD([sQuery(id+"F0.wireOp",EDGE,"E0.bottom")])]})])],"derivedFrom":makeQuery(id+"F3.opExtrude","CAP_FACE",FACE,{"disambiguationData":[OSD([subQ3,sQuery(id+"F2.wireOp",EDGE,"E345.top"),subQ5,subQ6,subQ4,sQuery(id+"F2.wireOp",EDGE,"E346.top"),subQ7,subQ8])],"isStart":false})}),makeQuery(id+"F6.opExtrude","CAP_FACE",FACE,{"disambiguationData":[OSD([sQuery(id+"F5.wireOp",EDGE,"E357"),sQuery(id+"F5.wireOp",EDGE,"E358"),sQuery(id+"F5.wireOp",EDGE,"E359"),sQuery(id+"F5.wireOp",EDGE,"E360")])],"isStart":true}),makeQuery(id+"F6.opExtrude","CAP_FACE",FACE,{"disambiguationData":[OSD([subQ0,sQuery(id+"F5.wireOp",EDGE,"E363.MirrorCS"),subQ1,subQ2])],"isStart":true})]})});}
            var Q2;
            {var subQ0=sQuery(id+"F5.wireOp",EDGE,"E367.MirrorCS");var subQ1=sQuery(id+"F5.wireOp",EDGE,"E370.MirrorCS");var subQ2=sQuery(id+"F5.wireOp",EDGE,"E372.MirrorCS");var subQ3=sQuery(id+"F2.wireOp",EDGE,"E345.top");var subQ4=sQuery(id+"F2.wireOp",EDGE,"E346.right");var subQ5=sQuery(id+"F2.wireOp",EDGE,"E345.left");var subQ6=sQuery(id+"F2.wireOp",EDGE,"E345.right");var subQ7=sQuery(id+"F2.wireOp",EDGE,"E346.top");var subQ8=sQuery(id+"F2.wireOp",EDGE,"E346.left");Q2=makeQuery(id+"F9.boolean.opBoolean","SPLIT",FACE,{"disambiguationData":[TD([makeQuery(id+"F6.opExtrude","SWEPT_FACE",FACE,{"disambiguationData":[OSD([subQ0])]})])],"derivedFrom":makeQuery(id+"F6.boolean.opBoolean","MERGE",FACE,{"derivedFrom":[makeQuery(id+"FBptylufdPnb45I_1.boolean.opBoolean","SPLIT",FACE,{"disambiguationData":[TD([makeQuery(id+"F1.opExtrude","SWEPT_FACE",FACE,{"disambiguationData":[OSD([sQuery(id+"F0.wireOp",EDGE,"E0.top")])]})])],"derivedFrom":makeQuery(id+"F3.opExtrude","CAP_FACE",FACE,{"disambiguationData":[OSD([sQuery(id+"F2.wireOp",EDGE,"E345.bottom"),subQ3,subQ5,subQ6,sQuery(id+"F2.wireOp",EDGE,"E346.bottom"),subQ7,subQ8,subQ4])],"isStart":false})}),makeQuery(id+"F6.opExtrude","CAP_FACE",FACE,{"disambiguationData":[OSD([sQuery(id+"F5.wireOp",EDGE,"E366.MirrorCS"),subQ0,subQ1,subQ2])],"isStart":true}),makeQuery(id+"F6.opExtrude","CAP_FACE",FACE,{"disambiguationData":[OSD([sQuery(id+"F5.wireOp",EDGE,"E368.MirrorCS"),sQuery(id+"F5.wireOp",EDGE,"E371.MirrorCS"),sQuery(id+"F5.wireOp",EDGE,"E373.MirrorCS"),sQuery(id+"F5.wireOp",EDGE,"E374.MirrorCS")])],"isStart":true})]})});}
            var Q3;
            {var subQ0=sQuery(id+"F5.wireOp",EDGE,"E368.MirrorCS");var subQ1=sQuery(id+"F5.wireOp",EDGE,"E373.MirrorCS");var subQ2=sQuery(id+"F5.wireOp",EDGE,"E374.MirrorCS");var subQ3=sQuery(id+"F2.wireOp",EDGE,"E345.top");var subQ4=sQuery(id+"F2.wireOp",EDGE,"E346.right");var subQ5=sQuery(id+"F2.wireOp",EDGE,"E345.left");var subQ6=sQuery(id+"F2.wireOp",EDGE,"E345.right");var subQ7=sQuery(id+"F2.wireOp",EDGE,"E346.top");var subQ8=sQuery(id+"F2.wireOp",EDGE,"E346.left");Q3=makeQuery(id+"F9.boolean.opBoolean","SPLIT",FACE,{"disambiguationData":[TD([makeQuery(id+"F6.opExtrude","SWEPT_FACE",FACE,{"disambiguationData":[OSD([subQ0])]})])],"derivedFrom":makeQuery(id+"F6.boolean.opBoolean","MERGE",FACE,{"derivedFrom":[makeQuery(id+"FBptylufdPnb45I_1.boolean.opBoolean","SPLIT",FACE,{"disambiguationData":[TD([makeQuery(id+"F1.opExtrude","SWEPT_FACE",FACE,{"disambiguationData":[OSD([sQuery(id+"F0.wireOp",EDGE,"E0.top")])]})])],"derivedFrom":makeQuery(id+"F3.opExtrude","CAP_FACE",FACE,{"disambiguationData":[OSD([sQuery(id+"F2.wireOp",EDGE,"E345.bottom"),subQ3,subQ5,subQ6,sQuery(id+"F2.wireOp",EDGE,"E346.bottom"),subQ7,subQ8,subQ4])],"isStart":false})}),makeQuery(id+"F6.opExtrude","CAP_FACE",FACE,{"disambiguationData":[OSD([sQuery(id+"F5.wireOp",EDGE,"E366.MirrorCS"),sQuery(id+"F5.wireOp",EDGE,"E367.MirrorCS"),sQuery(id+"F5.wireOp",EDGE,"E370.MirrorCS"),sQuery(id+"F5.wireOp",EDGE,"E372.MirrorCS")])],"isStart":true}),makeQuery(id+"F6.opExtrude","CAP_FACE",FACE,{"disambiguationData":[OSD([subQ0,sQuery(id+"F5.wireOp",EDGE,"E371.MirrorCS"),subQ1,subQ2])],"isStart":true})]})});}
            extrude(context, id + "F10", {"entities" : qUnion([Q0, Q1, Q2, Q3]), "operationType" : NewBodyOperationType.ADD, "depth" : 7 * mm});
        }
        {
            var Q0;
            {var subQ0=sQuery(id+"F5.wireOp",EDGE,"E359");Q0=makeQuery(id+"F10.boolean.opBoolean","MERGE",FACE,{"derivedFrom":[makeQuery(id+"F6.opExtrude","SWEPT_FACE",FACE,{"disambiguationData":[OSD([subQ0])]}),makeQuery(id+"F10.opExtrude","SWEPT_FACE",FACE,{"disambiguationData":[OSD([subQ0])]})]});}
            var sketch = newSketch(context, id + "F11", { "sketchPlane" : qUnion([Q0])});
            skLineSegment(sketch, "E396", {"start": v(-39.5, 120.63) * mm, "end": v(-35, 120.63) * mm});
            skLineSegment(sketch, "E397", {"start": v(-35, 120.63) * mm, "end": v(-35, 117.63) * mm});
            skLineSegment(sketch, "E398", {"start": v(-35, 117.63) * mm, "end": v(-39.5, 117.63) * mm});
            skLineSegment(sketch, "E399", {"start": v(-39.5, 117.63) * mm, "end": v(-39.5, 120.63) * mm});
            skSolve(sketch);
        }
        {
            var Q0;
            Q0 = qSketchRegion(id + "F11", true);
            extrude(context, id + "F12", {"entities" : qUnion([Q0]), "operationType" : NewBodyOperationType.ADD, "depth" : 2 * mm});
        }
        {
            var Q0;
            Q0=makeQuery(id+"F12.opExtrude","CAP_EDGE",EDGE,{"disambiguationData":[OSD([sQuery(id+"F11.wireOp",EDGE,"E399")])],"isStart":false});
            chamfer(context, id + "F13", {"entities" : qUnion([Q0]), "chamferType" : ChamferType.TWO_OFFSETS, "width1" : 2.5 * mm, "oppositeDirection" : false, "width2" : 2.5 * mm, "tangentPropagation" : true});
        }
        {
            var Q0;
            {var subQ0=sQuery(id+"F5.wireOp",EDGE,"E370.MirrorCS");Q0=makeQuery(id+"F10.boolean.opBoolean","MERGE",FACE,{"derivedFrom":[makeQuery(id+"F6.opExtrude","SWEPT_FACE",FACE,{"disambiguationData":[OSD([subQ0])]}),makeQuery(id+"F10.opExtrude","SWEPT_FACE",FACE,{"disambiguationData":[OSD([subQ0])]})]});}
            var sketch = newSketch(context, id + "F14", { "sketchPlane" : qUnion([Q0])});
            skLineSegment(sketch, "E400.bottom", {"start": v(-39.5, -60.37) * mm, "end": v(-35, -60.37) * mm});
            skLineSegment(sketch, "E400.top", {"start": v(-39.5, -63.37) * mm, "end": v(-35, -63.37) * mm});
            skLineSegment(sketch, "E400.left", {"start": v(-39.5, -60.37) * mm, "end": v(-39.5, -63.37) * mm});
            skLineSegment(sketch, "E400.right", {"start": v(-35, -60.37) * mm, "end": v(-35, -63.37) * mm});
            skSolve(sketch);
        }
        {
            var Q0;
            Q0 = qSketchRegion(id + "F14", true);
            extrude(context, id + "F15", {"entities" : qUnion([Q0]), "operationType" : NewBodyOperationType.ADD, "depth" : 2 * mm});
        }
        {
            var Q0;
            Q0=makeQuery(id+"F15.opExtrude","CAP_EDGE",EDGE,{"disambiguationData":[OSD([sQuery(id+"F14.wireOp",EDGE,"E400.left")])],"isStart":false});
            chamfer(context, id + "F16", {"entities" : qUnion([Q0]), "width" : 2.5 * mm, "tangentPropagation" : true});
        }
        {
            var Q0;
            {var subQ0=sQuery(id+"F5.wireOp",EDGE,"E362.MirrorCS");Q0=makeQuery(id+"F10.boolean.opBoolean","MERGE",FACE,{"derivedFrom":[makeQuery(id+"F6.opExtrude","SWEPT_FACE",FACE,{"disambiguationData":[OSD([subQ0])]}),makeQuery(id+"F10.opExtrude","SWEPT_FACE",FACE,{"disambiguationData":[OSD([subQ0])]})]});}
            var sketch = newSketch(context, id + "F17", { "sketchPlane" : qUnion([Q0])});
            skLineSegment(sketch, "E401.bottom", {"start": v(39.5, 120.63) * mm, "end": v(35, 120.63) * mm});
            skLineSegment(sketch, "E401.top", {"start": v(39.5, 117.63) * mm, "end": v(35, 117.63) * mm});
            skLineSegment(sketch, "E401.left", {"start": v(39.5, 120.63) * mm, "end": v(39.5, 117.63) * mm});
            skLineSegment(sketch, "E401.right", {"start": v(35, 120.63) * mm, "end": v(35, 117.63) * mm});
            skSolve(sketch);
        }
        {
            var Q0;
            Q0 = qSketchRegion(id + "F17", true);
            extrude(context, id + "F18", {"entities" : qUnion([Q0]), "operationType" : NewBodyOperationType.ADD, "depth" : 2 * mm});
        }
        {
            var Q0;
            Q0=makeQuery(id+"F18.opExtrude","CAP_EDGE",EDGE,{"disambiguationData":[OSD([sQuery(id+"F17.wireOp",EDGE,"E401.left")])],"isStart":false});
            chamfer(context, id + "F19", {"entities" : qUnion([Q0]), "width" : 2.5 * mm, "tangentPropagation" : true});
        }
        {
            var Q0;
            {var subQ0=sQuery(id+"F5.wireOp",EDGE,"E368.MirrorCS");Q0=makeQuery(id+"F10.boolean.opBoolean","MERGE",FACE,{"derivedFrom":[makeQuery(id+"F6.opExtrude","SWEPT_FACE",FACE,{"disambiguationData":[OSD([subQ0])]}),makeQuery(id+"F10.opExtrude","SWEPT_FACE",FACE,{"disambiguationData":[OSD([subQ0])]})]});}
            var sketch = newSketch(context, id + "F20", { "sketchPlane" : qUnion([Q0])});
            skLineSegment(sketch, "E402.bottom", {"start": v(39.5, -63.37) * mm, "end": v(35, -63.37) * mm});
            skLineSegment(sketch, "E402.top", {"start": v(39.5, -60.37) * mm, "end": v(35, -60.37) * mm});
            skLineSegment(sketch, "E402.left", {"start": v(39.5, -63.37) * mm, "end": v(39.5, -60.37) * mm});
            skLineSegment(sketch, "E402.right", {"start": v(35, -63.37) * mm, "end": v(35, -60.37) * mm});
            skSolve(sketch);
        }
        {
            var Q0;
            Q0 = qSketchRegion(id + "F20", true);
            extrude(context, id + "F21", {"entities" : qUnion([Q0]), "operationType" : NewBodyOperationType.ADD, "depth" : 2 * mm});
        }
        {
            var Q0;
            Q0=makeQuery(id+"F21.opExtrude","CAP_EDGE",EDGE,{"disambiguationData":[OSD([sQuery(id+"F20.wireOp",EDGE,"E402.left")])],"isStart":false});
            chamfer(context, id + "F22", {"entities" : qUnion([Q0]), "width" : 2.5 * mm, "tangentPropagation" : true});
        }
        {
            var Q0;
            Q0=makeQuery(id+"F4.imprint","IMPRINT",FACE,{"disambiguationData":[TD([[makeQuery(id+"F4.imprint","IMPRINT",EDGE,{"derivedFrom":sQuery(id+"F4.wireOp",EDGE,"E348")}),1.0]])]});
            extrude(context, id + "F23", {"entities" : qUnion([Q0]), "operationType" : NewBodyOperationType.REMOVE, "oppositeDirection" : true, "depth" : 107.5 * mm});
        }
    });
